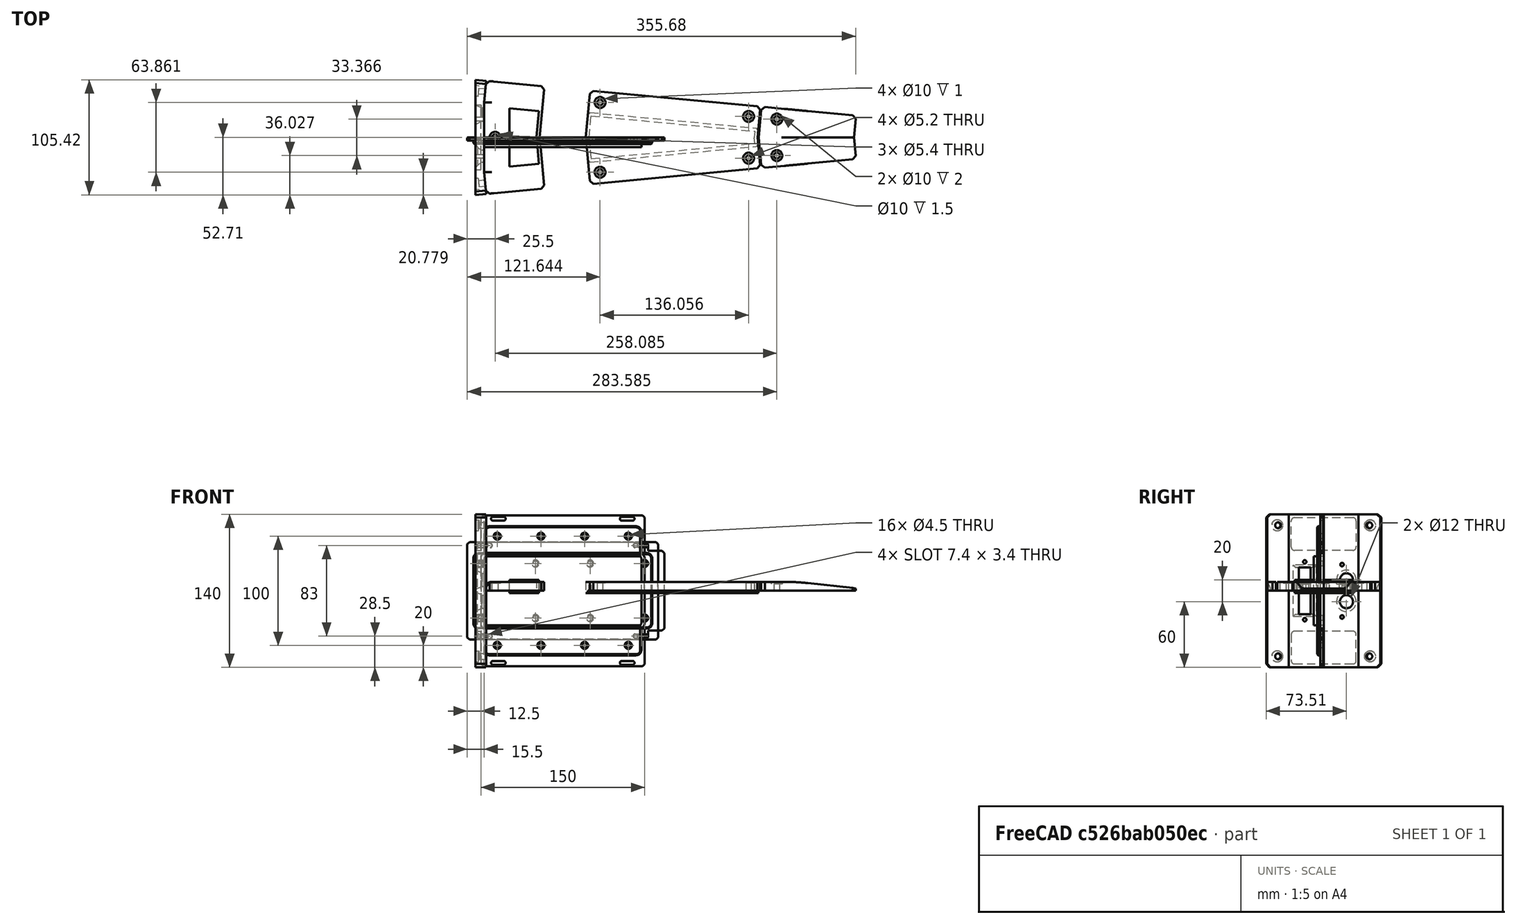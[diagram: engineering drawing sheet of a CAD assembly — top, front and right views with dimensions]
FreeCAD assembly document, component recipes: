
FREECAD ASSEMBLY — COMPONENT RECIPES ("RC-Robot-carters")

This assembly document has 8 components, labeled P0..P7 below (a component is one placed body or linked part). 8 of them carry a construction recipe — the FreeCAD feature program that regenerates the part from scratch, quoted from this document or its linked companion documents; the rest are supplied as boundary geometry only. No exploded tour is included for this assembly.
COMPONENT P0 — recipe-attached ("front-carter", modeled in this document).
Construction recipe (the document's own serialized feature program — sketch geometry with constraints, then the solid features built on it; lengths are millimeters unless a unit is written):

FEATURE [PartDesign::SubShapeBinder] Binder002
  BindCopyOnChange = 0
  BindMode = 0
  ClaimChildren = false
  Context = -> Body002 [Binder002.]
  Fuse = false
  MakeFace = true
  OffsetFill = false
  OffsetIntersection = false
  OffsetJoinType = 0
  OffsetOpenResult = false
  PartialLoad = false
  Refine = true
  Relative = true
  Support = -> [Link]
  _Version = 2
FEATURE [PartDesign::SubShapeBinder] Binder003
  BindCopyOnChange = 0
  BindMode = 0
  ClaimChildren = false
  Context = -> Body002 [Binder003.]
  Fuse = false
  MakeFace = true
  OffsetFill = false
  OffsetIntersection = false
  OffsetJoinType = 0
  OffsetOpenResult = false
  PartialLoad = false
  Refine = true
  Relative = true
  Support = -> [Part[Body.Mirrored.Face32]]
  _Version = 2
FEATURE [Sketcher::SketchObject] Sketch004
  ArcFitTolerance = 1e-06
  AttachmentSupport = -> [Origin006]
  ExternalGeometry = -> [Binder002,Binder003]
  ExternalTypes = [0,0,0,0,0,0]
  FullyConstrained = true
  MakeInternals = false
  MapMode = 5
  sketch-geometry (7):
    g0: LineSegment StartX=268.466 StartY=19.9119 StartZ=0 EndX=182.088 EndY=28.0449 EndZ=0
    g1: LineSegment StartX=182.088 StartY=28.0449 StartZ=0 EndX=179.448 EndY=0 EndZ=0
    g2: LineSegment StartX=179.448 StartY=0 StartZ=0 EndX=266.591 EndY=0 EndZ=0
    g3: LineSegment StartX=266.591 StartY=0 StartZ=0 EndX=268.466 EndY=19.9119 EndZ=0
    g4: Circle CenterX=196.085 CenterY=16.6828 CenterZ=0 NormalX=0 NormalY=0 NormalZ=1 AngleXU=0 Radius=2.7
    g5: GeomPoint X=180.214 Y=8.13298 Z=0
    g6: LineSegment [constr] StartX=196.085 StartY=16.6828 StartZ=0 EndX=197.022 EndY=26.6388 EndZ=0
  constraints (19):
    c: PointOnObject(g0,g-5)
    c: Coincident(g0,g1)
    c: PointOnObject(g1,g-1)
    c: Coincident(g2,g1)
    c: Coincident(g2,g-5)
    c: Coincident(g3,g2)
    c: Coincident(g3,g0)
    c: Parallel(g0,g-6)
    c: Perpendicular(g0,g1)
    c: Distance(g1,g-8) = 1
    c: Distance(g3,g3) = 20
    c: Diameter(g4) = 5.4
    c: PointOnObject(g5,g-3)
    c: PointOnObject(g5,g1)
    c: Coincident(g6,g4)
    c: Distance(g6,g6) = 10
    c: Perpendicular(g0,g6)
    c: PointOnObject(g6,g0)
    c: Distance(g6,g1) = 15
FEATURE [PartDesign::Pad] Pad003
  Direction = (0,0,1)
  Length = 8.2
  Length2 = 10
  Profile = -> Sketch004
  ReferenceAxis = -> Sketch004 [N_Axis]
  Refine = true
  SideType = 0
  Suppressed = false
  Type = 0
  Type2 = 0
FEATURE [Sketcher::SketchObject] Sketch005
  ArcFitTolerance = 1e-06
  AttachmentSupport = -> [Pad003]
  ExternalGeometry = -> [Pad003]
  ExternalTypes = [0]
  FullyConstrained = true
  MakeInternals = false
  MapMode = 5
  Placement = pos=(0,0,8.2) rot=(0,0,1;0rad)
  sketch-geometry (1):
    g0: Circle CenterX=196.085 CenterY=16.6828 CenterZ=0 NormalX=0 NormalY=0 NormalZ=1 AngleXU=0 Radius=5
  constraints (2):
    c: Coincident(g0,g-3)
    c: Diameter(g0) = 10
FEATURE [PartDesign::Pocket] Pocket001
  BaseFeature = -> Pad003
  Direction = (0,0,-1)
  Length = 2
  Length2 = 5
  Profile = -> Sketch005
  ReferenceAxis = -> Sketch005 [N_Axis]
  Refine = true
  SideType = 0
  Suppressed = false
  Type = 0
  Type2 = 0
FEATURE [PartDesign::Chamfer] Chamfer002
  Angle = 45
  Base = -> Pocket001 [Edge2]
  BaseFeature = -> Pocket001
  ChamferType = 0
  FlipDirection = false
  Refine = true
  Size = 3
  Size2 = 1
  SupportTransform = false
  Suppressed = false
  UseAllEdges = false
FEATURE [PartDesign::Chamfer] Chamfer003
  Angle = 45
  Base = -> Chamfer002 [Edge13]
  BaseFeature = -> Chamfer002
  ChamferType = 1
  FlipDirection = false
  Refine = true
  Size = 6
  Size2 = 55
  SupportTransform = false
  Suppressed = false
  UseAllEdges = false
FEATURE [PartDesign::Fillet] Fillet
  Base = -> Chamfer003 [Edge10]
  BaseFeature = -> Chamfer003
  Radius = 200
  Refine = true
  SupportTransform = false
  Suppressed = false
  UseAllEdges = false
FEATURE [PartDesign::Chamfer] Chamfer004
  Angle = 45
  Base = -> Fillet [Edge3]
  BaseFeature = -> Fillet
  ChamferType = 0
  FlipDirection = false
  Refine = true
  Size = 3
  Size2 = 1
  SupportTransform = false
  Suppressed = false
  UseAllEdges = false
FEATURE [PartDesign::Mirrored] Mirrored001
  BaseFeature = -> Chamfer004
  MirrorPlane = -> Chamfer004 [Face9]
  Refine = true
  Suppressed = false
  TransformMode = 1
FEATURE [PartDesign::Body] Body002  label="front-carter"
  AllowCompound = true
  Group = -> [Binder002,Sketch004,Binder003,Pad003,Sketch005,Pocket001,Chamfer002,Chamfer003,Fillet,Chamfer004,Mirrored001]
  Origin = -> Origin006
  Tip = -> Mirrored001
COMPONENT P1 — recipe-attached ("top-carter-core001", modeled in this document).
Construction recipe (the document's own serialized feature program — sketch geometry with constraints, then the solid features built on it; lengths are millimeters unless a unit is written):

FEATURE [Sketcher::SketchObject] Sketch022
  ArcFitTolerance = 1e-06
  AttachmentSupport = -> [Origin026]
  ExternalTypes = [0]
  FullyConstrained = true
  MakeInternals = false
  MapMode = 5
  Placement = pos=(0,0,0) rot=(1,0,0;1.5708rad)
  sketch-geometry (13):
    g0: LineSegment [constr] StartX=-87.5 StartY=-45 StartZ=0 EndX=87.5 EndY=-45 EndZ=0
    g1: LineSegment [constr] StartX=87.5 StartY=-45 StartZ=0 EndX=87.5 EndY=45 EndZ=0
    g2: LineSegment [constr] StartX=87.5 StartY=45 StartZ=0 EndX=-87.5 EndY=45 EndZ=0
    g3: LineSegment [constr] StartX=-87.5 StartY=45 StartZ=0 EndX=-87.5 EndY=-45 EndZ=0
    g4: GeomPoint [constr] X=0 Y=0 Z=0
    g5: LineSegment [constr] StartX=-87.5 StartY=-44.6 StartZ=0 EndX=87.5 EndY=-44.6 EndZ=0
    g6: LineSegment StartX=87.5 StartY=-44.6 StartZ=0 EndX=87.5 EndY=44.6 EndZ=0
    g7: LineSegment [constr] StartX=87.5 StartY=44.6 StartZ=0 EndX=-87.5 EndY=44.6 EndZ=0
    g8: LineSegment [constr] StartX=-87.5 StartY=44.6 StartZ=0 EndX=-87.5 EndY=-44.6 EndZ=0
    g9: GeomPoint [constr] X=0 Y=0 Z=0
    g10: LineSegment StartX=-2e-15 StartY=-44.6 StartZ=0 EndX=-2e-15 EndY=44.6 EndZ=0
    g11: LineSegment StartX=-2e-15 StartY=44.6 StartZ=0 EndX=87.5 EndY=44.6 EndZ=0
    g12: LineSegment StartX=-2e-15 StartY=-44.6 StartZ=0 EndX=87.5 EndY=-44.6 EndZ=0
  constraints (30):
    c: Coincident(g0,g1)
    c: Coincident(g1,g2)
    c: Coincident(g2,g3)
    c: Coincident(g3,g0)
    c: Horizontal(g0)
    c: Horizontal(g2)
    c: Vertical(g1)
    c: Vertical(g3)
    c: Symmetric(g2,g0,g4)
    c: Coincident(g4,g-1)
    c: DistanceX(g2,g2) = 175
    c: DistanceY(g1,g1) = 90
    c: Coincident(g5,g6)
    c: Coincident(g6,g7)
    c: Coincident(g7,g8)
    c: Coincident(g8,g5)
    c: Horizontal(g5)
    c: Horizontal(g7)
    c: Vertical(g6)
    c: Vertical(g8)
    c: Symmetric(g7,g5,g9)
    c: Coincident(g9,g4)
    c: PointOnObject(g6,g1)
    c: Distance(g6,g1) = 0.4
    c: Symmetric(g5,g5,g10)
    c: Symmetric(g7,g7,g10)
    c: Coincident(g11,g10)
    c: Coincident(g11,g6)
    c: Coincident(g12,g10)
    c: Coincident(g12,g5)
FEATURE [PartDesign::Pad] Pad013
  Direction = (0,-1,2e-16)
  Length = 3
  Length2 = 10
  Profile = -> Sketch022
  ReferenceAxis = -> Sketch022 [N_Axis]
  Refine = true
  SideType = 0
  Suppressed = false
  Type = 0
  Type2 = 0
FEATURE [Sketcher::SketchObject] Sketch023
  ArcFitTolerance = 1e-06
  AttachmentSupport = -> [Origin026]
  ExternalGeometry = -> [Pad013]
  ExternalTypes = [0,0]
  FullyConstrained = true
  MakeInternals = false
  MapMode = 5
  Placement = pos=(0,0,0) rot=(1,0,0;1.5708rad)
  sketch-geometry (6):
    g0: ArcOfCircle CenterX=76.5 CenterY=41.5 CenterZ=0 NormalX=0 NormalY=0 NormalZ=1 AngleXU=0 Radius=1.7 StartAngle=4.71239 EndAngle=7.85398
    g1: ArcOfCircle CenterX=66.5 CenterY=41.5 CenterZ=0 NormalX=0 NormalY=0 NormalZ=1 AngleXU=0 Radius=1.7 StartAngle=1.5708 EndAngle=4.71239
    g2: LineSegment StartX=76.5 StartY=39.8 StartZ=0 EndX=66.5 EndY=39.8 EndZ=0
    g3: LineSegment StartX=76.5 StartY=43.2 StartZ=0 EndX=66.5 EndY=43.2 EndZ=0
    g4: LineSegment [constr] StartX=66.5 StartY=41.5 StartZ=0 EndX=76.5 EndY=41.5 EndZ=0
    g5: GeomPoint [constr] X=71.5 Y=41.5 Z=0
  constraints (13):
    c: Tangent(g0,g2) = 1.5708
    c: Tangent(g0,g3) = -1.5708
    c: Tangent(g1,g2) = 1.5708
    c: Tangent(g1,g3) = -1.5708
    c: Equal(g0,g1)
    c: Horizontal(g3)
    c: DistanceX(g1,g0) = 10
    c: Radius(g0) = 1.7
    c: DistanceY(g-1,g0) = 41.5
    c: Coincident(g4,g1)
    c: Coincident(g4,g0)
    c: Symmetric(g4,g4,g5)
    c: Distance(g5,g-3) = 16
FEATURE [PartDesign::Pocket] Pocket010
  BaseFeature = -> Pad013
  Direction = (0,1,-2e-16)
  Length = 5
  Length2 = 5
  Profile = -> Sketch023
  ReferenceAxis = -> Sketch023 [N_Axis]
  Refine = true
  Reversed = true
  SideType = 0
  Suppressed = false
  Type = 0
  Type2 = 0
FEATURE [PartDesign::Mirrored] Mirrored008
  BaseFeature = -> Pocket010
  MirrorPlane = -> XY_Plane013
  Originals = -> [Pocket010]
  Refine = true
  Suppressed = false
  TransformMode = 0
FEATURE [PartDesign::Mirrored] Mirrored009
  BaseFeature = -> Mirrored008
  MirrorPlane = -> YZ_Plane013
  Refine = true
  Suppressed = false
  TransformMode = 1
FEATURE [PartDesign::Chamfer] Chamfer013
  Angle = 45
  Base = -> Mirrored009 [Edge8,Edge6,Edge2,Edge1]
  BaseFeature = -> Mirrored009
  ChamferType = 0
  FlipDirection = false
  Refine = true
  Size = 2
  Size2 = 1
  SupportTransform = false
  Suppressed = false
  UseAllEdges = false
FEATURE [Sketcher::SketchObject] Sketch025
  ArcFitTolerance = 1e-06
  ExternalTypes = [0,0]
  FullyConstrained = true
  MakeInternals = false
  MapMode = 5
  Placement = pos=(0,-3,0) rot=(1,0,0;1.5708rad)
  sketch-geometry (5):
    g0: LineSegment StartX=-82 StartY=-34.6 StartZ=0 EndX=82 EndY=-34.6 EndZ=0
    g1: LineSegment StartX=82 StartY=-34.6 StartZ=0 EndX=82 EndY=34.6 EndZ=0
    g2: LineSegment StartX=82 StartY=34.6 StartZ=0 EndX=-82 EndY=34.6 EndZ=0
    g3: LineSegment StartX=-82 StartY=34.6 StartZ=0 EndX=-82 EndY=-34.6 EndZ=0
    g4: GeomPoint [constr] X=0 Y=0 Z=0
  constraints (12):
    c: Coincident(g0,g1)
    c: Coincident(g1,g2)
    c: Coincident(g2,g3)
    c: Coincident(g3,g0)
    c: Horizontal(g0)
    c: Horizontal(g2)
    c: Vertical(g1)
    c: Vertical(g3)
    c: Symmetric(g2,g0,g4)
    c: Coincident(g4,g-1)
    c: Distance(g-3,g3) = 3
    c: Distance(g-4,g2) = 10
FEATURE [PartDesign::Pad] Pad015
  BaseFeature = -> Chamfer013
  Direction = (0,-1,2e-16)
  Length = 3
  Length2 = 10
  Profile = -> Sketch025
  ReferenceAxis = -> Sketch025 [N_Axis]
  Refine = true
  SideType = 0
  Suppressed = false
  Type = 0
  Type2 = 0
FEATURE [PartDesign::Fillet] Fillet004
  Base = -> Pad015 [Edge80,Edge78,Edge82,Edge77]
  BaseFeature = -> Pad015
  Radius = 5
  Refine = true
  SupportTransform = false
  Suppressed = false
  UseAllEdges = false
FEATURE [Sketcher::SketchObject] Sketch026
  ArcFitTolerance = 1e-06
  AttachmentSupport = -> [Fillet004]
  ExternalTypes = [0]
  FullyConstrained = true
  MakeInternals = true
  MapMode = 5
  Placement = pos=(0,-6,0) rot=(1,0,0;1.5708rad)
  sketch-geometry (19):
    g0: LineSegment [constr] StartX=-75 StartY=25 StartZ=0 EndX=-75 EndY=-25 EndZ=0
    g1: LineSegment [constr] StartX=-75 StartY=-25 StartZ=0 EndX=-25 EndY=-25 EndZ=0
    g2: LineSegment [constr] StartX=-25 StartY=-25 StartZ=0 EndX=-25 EndY=25 EndZ=0
    g3: LineSegment [constr] StartX=-25 StartY=25 StartZ=0 EndX=-75 EndY=25 EndZ=0
    g4: GeomPoint [constr] X=-50 Y=0 Z=0
    g5: LineSegment [constr] StartX=25 StartY=25 StartZ=0 EndX=25 EndY=-25 EndZ=0
    g6: LineSegment [constr] StartX=25 StartY=-25 StartZ=0 EndX=75 EndY=-25 EndZ=0
    g7: LineSegment [constr] StartX=75 StartY=-25 StartZ=0 EndX=75 EndY=25 EndZ=0
    g8: LineSegment [constr] StartX=75 StartY=25 StartZ=0 EndX=25 EndY=25 EndZ=0
    g9: GeomPoint [constr] X=50 Y=0 Z=0
    g10: LineSegment [constr] StartX=-25 StartY=25 StartZ=0 EndX=25 EndY=25 EndZ=0
    g11: Circle CenterX=-75 CenterY=25 CenterZ=0 NormalX=0 NormalY=0 NormalZ=1 AngleXU=0 Radius=2.25
    g12: Circle CenterX=-25 CenterY=25 CenterZ=0 NormalX=0 NormalY=0 NormalZ=1 AngleXU=0 Radius=2.25
    g13: Circle CenterX=25 CenterY=25 CenterZ=0 NormalX=0 NormalY=0 NormalZ=1 AngleXU=0 Radius=2.25
    g14: Circle CenterX=75 CenterY=25 CenterZ=0 NormalX=0 NormalY=0 NormalZ=1 AngleXU=0 Radius=2.25
    g15: Circle CenterX=75 CenterY=-25 CenterZ=0 NormalX=0 NormalY=0 NormalZ=1 AngleXU=0 Radius=2.25
    g16: Circle CenterX=25 CenterY=-25 CenterZ=0 NormalX=0 NormalY=0 NormalZ=1 AngleXU=0 Radius=2.25
    g17: Circle CenterX=-25 CenterY=-25 CenterZ=0 NormalX=0 NormalY=0 NormalZ=1 AngleXU=0 Radius=2.25
    g18: Circle CenterX=-75 CenterY=-25 CenterZ=0 NormalX=0 NormalY=0 NormalZ=1 AngleXU=0 Radius=2.25
  constraints (43):
    c: Coincident(g0,g1)
    c: Coincident(g1,g2)
    c: Coincident(g2,g3)
    c: Coincident(g3,g0)
    c: Vertical(g0)
    c: Vertical(g2)
    c: Horizontal(g1)
    c: Horizontal(g3)
    c: Symmetric(g2,g0,g4)
    c: PointOnObject(g4,g-1)
    c: Coincident(g5,g6)
    c: Coincident(g6,g7)
    c: Coincident(g7,g8)
    c: Coincident(g8,g5)
    c: Vertical(g5)
    c: Vertical(g7)
    c: Horizontal(g6)
    c: Horizontal(g8)
    c: Symmetric(g7,g5,g9)
    c: PointOnObject(g9,g-1)
    c: Symmetric(g2,g5,g-2)
    c: Equal(g3,g5)
    c: Equal(g5,g8)
    c: Coincident(g10,g2)
    c: Coincident(g10,g5)
    c: Equal(g10,g8)
    c: DistanceY(g7,g7) = 50
    c: Coincident(g11,g0)
    c: Coincident(g12,g2)
    c: Coincident(g13,g5)
    c: Coincident(g14,g7)
    c: Coincident(g15,g6)
    c: Coincident(g16,g5)
    c: Coincident(g17,g1)
    c: Coincident(g18,g0)
    c: Equal(g18,g11)
    c: Equal(g11,g12)
    c: Equal(g12,g17)
    c: Equal(g17,g13)
    c: Equal(g13,g16)
    c: Equal(g16,g15)
    c: Equal(g15,g14)
    c: Diameter(g14) = 4.5
FEATURE [PartDesign::Pocket] Pocket011
  BaseFeature = -> Fillet004
  Direction = (0,1,-2e-16)
  Length = 7
  Length2 = 5
  Profile = -> Sketch026
  ReferenceAxis = -> Sketch026 [N_Axis]
  Refine = true
  SideType = 0
  Suppressed = false
  Type = 0
  Type2 = 0
FEATURE [PartDesign::Chamfer] Chamfer014
  Angle = 45
  Base = -> Pocket011 [Face34]
  BaseFeature = -> Pocket011
  ChamferType = 0
  FlipDirection = false
  Refine = true
  Size = 1
  Size2 = 1
  SupportTransform = false
  Suppressed = false
  UseAllEdges = false
FEATURE [PartDesign::Chamfer] Chamfer015
  Angle = 45
  Base = -> Chamfer014 [Face51]
  BaseFeature = -> Chamfer014
  ChamferType = 0
  FlipDirection = false
  Refine = true
  Size = 0.4
  Size2 = 1
  SupportTransform = false
  Suppressed = false
  UseAllEdges = false
FEATURE [PartDesign::Body] Body009  label="top-carter-core001"
  AllowCompound = true
  Group = -> [Sketch022,Pad013,Sketch023,Pocket010,Mirrored008,Mirrored009,Chamfer013,Sketch025,Pad015,Fillet004,Sketch026,Pocket011,Chamfer014,Chamfer015]
  Origin = -> Origin026
  Tip = -> Chamfer015
COMPONENT P2 — recipe-attached ("top-carter-core002", modeled in this document).
Construction recipe (the document's own serialized feature program — sketch geometry with constraints, then the solid features built on it; lengths are millimeters unless a unit is written):

FEATURE [Sketcher::SketchObject] Sketch027
  ArcFitTolerance = 1e-06
  AttachmentSupport = -> [Origin028]
  ExternalTypes = [0]
  FullyConstrained = true
  MakeInternals = false
  MapMode = 5
  Placement = pos=(0,0,0) rot=(1,0,0;1.5708rad)
  sketch-geometry (13):
    g0: LineSegment [constr] StartX=-75 StartY=-69.5 StartZ=0 EndX=75 EndY=-69.5 EndZ=0
    g1: LineSegment [constr] StartX=75 StartY=-69.5 StartZ=0 EndX=75 EndY=69.5 EndZ=0
    g2: LineSegment [constr] StartX=75 StartY=69.5 StartZ=0 EndX=-75 EndY=69.5 EndZ=0
    g3: LineSegment [constr] StartX=-75 StartY=69.5 StartZ=0 EndX=-75 EndY=-69.5 EndZ=0
    g4: GeomPoint [constr] X=0 Y=0 Z=0
    g5: LineSegment [constr] StartX=-75 StartY=-69.1 StartZ=0 EndX=75 EndY=-69.1 EndZ=0
    g6: LineSegment StartX=75 StartY=-69.1 StartZ=0 EndX=75 EndY=69.1 EndZ=0
    g7: LineSegment [constr] StartX=75 StartY=69.1 StartZ=0 EndX=-75 EndY=69.1 EndZ=0
    g8: LineSegment [constr] StartX=-75 StartY=69.1 StartZ=0 EndX=-75 EndY=-69.1 EndZ=0
    g9: GeomPoint [constr] X=0 Y=0 Z=0
    g10: LineSegment StartX=3.7e-15 StartY=-69.1 StartZ=0 EndX=3.7e-15 EndY=69.1 EndZ=0
    g11: LineSegment StartX=3.7e-15 StartY=69.1 StartZ=0 EndX=75 EndY=69.1 EndZ=0
    g12: LineSegment StartX=3.7e-15 StartY=-69.1 StartZ=0 EndX=75 EndY=-69.1 EndZ=0
  constraints (30):
    c: Coincident(g0,g1)
    c: Coincident(g1,g2)
    c: Coincident(g2,g3)
    c: Coincident(g3,g0)
    c: Horizontal(g0)
    c: Horizontal(g2)
    c: Vertical(g1)
    c: Vertical(g3)
    c: Symmetric(g2,g0,g4)
    c: Coincident(g4,g-1)
    c: DistanceX(g2,g2) = 150
    c: DistanceY(g1,g1) = 139
    c: Coincident(g5,g6)
    c: Coincident(g6,g7)
    c: Coincident(g7,g8)
    c: Coincident(g8,g5)
    c: Horizontal(g5)
    c: Horizontal(g7)
    c: Vertical(g6)
    c: Vertical(g8)
    c: Symmetric(g7,g5,g9)
    c: Coincident(g9,g4)
    c: PointOnObject(g6,g1)
    c: Distance(g6,g1) = 0.4
    c: Symmetric(g5,g5,g10)
    c: Symmetric(g7,g7,g10)
    c: Coincident(g11,g10)
    c: Coincident(g11,g6)
    c: Coincident(g12,g10)
    c: Coincident(g12,g5)
FEATURE [PartDesign::Pad] Pad016
  Direction = (0,-1,2e-16)
  Length = 3
  Length2 = 10
  Profile = -> Sketch027
  ReferenceAxis = -> Sketch027 [N_Axis]
  Refine = true
  SideType = 0
  Suppressed = false
  Type = 0
  Type2 = 0
FEATURE [Sketcher::SketchObject] Sketch028
  ArcFitTolerance = 1e-06
  AttachmentSupport = -> [Origin028]
  ExternalGeometry = -> [Pad016]
  ExternalTypes = [0,0]
  FullyConstrained = true
  MakeInternals = false
  MapMode = 5
  Placement = pos=(0,0,0) rot=(1,0,0;1.5708rad)
  sketch-geometry (6):
    g0: ArcOfCircle CenterX=64 CenterY=66 CenterZ=0 NormalX=0 NormalY=0 NormalZ=1 AngleXU=0 Radius=1.7 StartAngle=4.71239 EndAngle=7.85398
    g1: ArcOfCircle CenterX=54 CenterY=66 CenterZ=0 NormalX=0 NormalY=0 NormalZ=1 AngleXU=0 Radius=1.7 StartAngle=1.5708 EndAngle=4.71239
    g2: LineSegment StartX=64 StartY=64.3 StartZ=0 EndX=54 EndY=64.3 EndZ=0
    g3: LineSegment StartX=64 StartY=67.7 StartZ=0 EndX=54 EndY=67.7 EndZ=0
    g4: LineSegment [constr] StartX=54 StartY=66 StartZ=0 EndX=64 EndY=66 EndZ=0
    g5: GeomPoint [constr] X=59 Y=66 Z=0
  constraints (13):
    c: Tangent(g0,g2) = 1.5708
    c: Tangent(g0,g3) = -1.5708
    c: Tangent(g1,g2) = 1.5708
    c: Tangent(g1,g3) = -1.5708
    c: Equal(g0,g1)
    c: Horizontal(g3)
    c: DistanceX(g1,g0) = 10
    c: Radius(g0) = 1.7
    c: Coincident(g4,g1)
    c: Coincident(g4,g0)
    c: Symmetric(g4,g4,g5)
    c: Distance(g5,g-3) = 16
    c: Distance(g-4,g4) = 3.1
FEATURE [PartDesign::Pocket] Pocket012
  BaseFeature = -> Pad016
  Direction = (0,1,-2e-16)
  Length = 5
  Length2 = 5
  Profile = -> Sketch028
  ReferenceAxis = -> Sketch028 [N_Axis]
  Refine = true
  Reversed = true
  SideType = 0
  Suppressed = false
  Type = 0
  Type2 = 0
FEATURE [PartDesign::Mirrored] Mirrored010
  BaseFeature = -> Pocket012
  MirrorPlane = -> XY_Plane014
  Originals = -> [Pocket012]
  Refine = true
  Suppressed = false
  TransformMode = 0
FEATURE [PartDesign::Mirrored] Mirrored011
  BaseFeature = -> Mirrored010
  MirrorPlane = -> YZ_Plane014
  Refine = true
  Suppressed = false
  TransformMode = 1
FEATURE [PartDesign::Chamfer] Chamfer016
  Angle = 45
  Base = -> Mirrored011 [Edge6,Edge1,Edge8,Edge2]
  BaseFeature = -> Mirrored011
  ChamferType = 0
  FlipDirection = false
  Refine = true
  Size = 2
  Size2 = 1
  SupportTransform = false
  Suppressed = false
  UseAllEdges = false
FEATURE [Sketcher::SketchObject] Sketch029
  ArcFitTolerance = 1e-06
  AttachmentSupport = -> [Chamfer016]
  ExternalGeometry = -> [Chamfer016]
  ExternalTypes = [0,0]
  FullyConstrained = true
  MakeInternals = false
  MapMode = 5
  Placement = pos=(0,-3,7e-16) rot=(1,0,0;1.5708rad)
  sketch-geometry (5):
    g0: LineSegment StartX=-72 StartY=-59.1 StartZ=0 EndX=72 EndY=-59.1 EndZ=0
    g1: LineSegment StartX=72 StartY=-59.1 StartZ=0 EndX=72 EndY=59.1 EndZ=0
    g2: LineSegment StartX=72 StartY=59.1 StartZ=0 EndX=-72 EndY=59.1 EndZ=0
    g3: LineSegment StartX=-72 StartY=59.1 StartZ=0 EndX=-72 EndY=-59.1 EndZ=0
    g4: GeomPoint [constr] X=0 Y=0 Z=0
  constraints (12):
    c: Coincident(g0,g1)
    c: Coincident(g1,g2)
    c: Coincident(g2,g3)
    c: Coincident(g3,g0)
    c: Horizontal(g0)
    c: Horizontal(g2)
    c: Vertical(g1)
    c: Vertical(g3)
    c: Symmetric(g2,g0,g4)
    c: Coincident(g4,g-1)
    c: Distance(g-3,g2) = 10
    c: Distance(g-4,g3) = 3
FEATURE [PartDesign::Pad] Pad017
  BaseFeature = -> Chamfer016
  Direction = (0,-1,2e-16)
  Length = 3
  Length2 = 10
  Profile = -> Sketch029
  ReferenceAxis = -> Sketch029 [N_Axis]
  Refine = true
  SideType = 0
  Suppressed = false
  Type = 0
  Type2 = 0
FEATURE [PartDesign::Fillet] Fillet005
  Base = -> Pad017 [Edge78,Edge80,Edge77,Edge82]
  BaseFeature = -> Pad017
  Radius = 5
  Refine = true
  SupportTransform = false
  Suppressed = false
  UseAllEdges = false
FEATURE [Sketcher::SketchObject] Sketch030
  ArcFitTolerance = 1e-06
  AttachmentSupport = -> [Fillet005]
  ExternalGeometry = -> [Fillet005]
  ExternalTypes = [0,0]
  FullyConstrained = true
  MakeInternals = true
  MapMode = 5
  Placement = pos=(0,-6,1.4e-15) rot=(1,0,0;1.5708rad)
  sketch-geometry (19):
    g0: LineSegment [constr] StartX=-60 StartY=50 StartZ=0 EndX=-60 EndY=-50 EndZ=0
    g1: LineSegment [constr] StartX=-60 StartY=-50 StartZ=0 EndX=-20 EndY=-50 EndZ=0
    g2: LineSegment [constr] StartX=-20 StartY=-50 StartZ=0 EndX=-20 EndY=50 EndZ=0
    g3: LineSegment [constr] StartX=-20 StartY=50 StartZ=0 EndX=-60 EndY=50 EndZ=0
    g4: GeomPoint [constr] X=-40 Y=0 Z=0
    g5: LineSegment [constr] StartX=20 StartY=50 StartZ=0 EndX=20 EndY=-50 EndZ=0
    g6: LineSegment [constr] StartX=20 StartY=-50 StartZ=0 EndX=60 EndY=-50 EndZ=0
    g7: LineSegment [constr] StartX=60 StartY=-50 StartZ=0 EndX=60 EndY=50 EndZ=0
    g8: LineSegment [constr] StartX=60 StartY=50 StartZ=0 EndX=20 EndY=50 EndZ=0
    g9: GeomPoint [constr] X=40 Y=0 Z=0
    g10: LineSegment [constr] StartX=-20 StartY=50 StartZ=0 EndX=20 EndY=50 EndZ=0
    g11: Circle CenterX=-60 CenterY=50 CenterZ=0 NormalX=0 NormalY=0 NormalZ=1 AngleXU=0 Radius=2.25
    g12: Circle CenterX=-20 CenterY=50 CenterZ=0 NormalX=0 NormalY=0 NormalZ=1 AngleXU=0 Radius=2.25
    g13: Circle CenterX=20 CenterY=50 CenterZ=0 NormalX=0 NormalY=0 NormalZ=1 AngleXU=0 Radius=2.25
    g14: Circle CenterX=60 CenterY=50 CenterZ=0 NormalX=0 NormalY=0 NormalZ=1 AngleXU=0 Radius=2.25
    g15: Circle CenterX=60 CenterY=-50 CenterZ=0 NormalX=0 NormalY=0 NormalZ=1 AngleXU=0 Radius=2.25
    g16: Circle CenterX=20 CenterY=-50 CenterZ=0 NormalX=0 NormalY=0 NormalZ=1 AngleXU=0 Radius=2.25
    g17: Circle CenterX=-20 CenterY=-50 CenterZ=0 NormalX=0 NormalY=0 NormalZ=1 AngleXU=0 Radius=2.25
    g18: Circle CenterX=-60 CenterY=-50 CenterZ=0 NormalX=0 NormalY=0 NormalZ=1 AngleXU=0 Radius=2.25
  constraints (43):
    c: Coincident(g0,g1)
    c: Coincident(g1,g2)
    c: Coincident(g2,g3)
    c: Coincident(g3,g0)
    c: Vertical(g0)
    c: Vertical(g2)
    c: Horizontal(g1)
    c: Horizontal(g3)
    c: Symmetric(g2,g0,g4)
    c: PointOnObject(g4,g-1)
    c: Coincident(g5,g6)
    c: Coincident(g6,g7)
    c: Coincident(g7,g8)
    c: Coincident(g8,g5)
    c: Vertical(g5)
    c: Vertical(g7)
    c: Horizontal(g6)
    c: Horizontal(g8)
    c: Symmetric(g7,g5,g9)
    c: PointOnObject(g9,g-1)
    c: Symmetric(g2,g5,g-2)
    c: Coincident(g10,g2)
    c: Coincident(g10,g5)
    c: Equal(g10,g8)
    c: DistanceY(g7,g7) = 100
    c: Coincident(g11,g0)
    c: Coincident(g12,g2)
    c: Coincident(g13,g5)
    c: Coincident(g14,g7)
    c: Coincident(g15,g6)
    c: Coincident(g16,g5)
    c: Coincident(g17,g1)
    c: Coincident(g18,g0)
    c: Equal(g18,g11)
    c: Equal(g11,g12)
    c: Equal(g12,g17)
    c: Equal(g17,g13)
    c: Equal(g13,g16)
    c: Equal(g16,g15)
    c: Equal(g15,g14)
    c: Diameter(g14) = 4.5
    c: Equal(g3,g10)
    c: DistanceX(g8,g8) = 40
FEATURE [PartDesign::Pocket] Pocket013
  BaseFeature = -> Fillet005
  Direction = (0,1,-2e-16)
  Length = 7
  Length2 = 5
  Profile = -> Sketch030
  ReferenceAxis = -> Sketch030 [N_Axis]
  Refine = true
  SideType = 0
  Suppressed = false
  Type = 0
  Type2 = 0
FEATURE [PartDesign::Chamfer] Chamfer017
  Angle = 45
  Base = -> Pocket013 [Face34]
  BaseFeature = -> Pocket013
  ChamferType = 0
  FlipDirection = false
  Refine = true
  Size = 1
  Size2 = 1
  SupportTransform = false
  Suppressed = false
  UseAllEdges = false
FEATURE [PartDesign::Chamfer] Chamfer018
  Angle = 45
  Base = -> Chamfer017 [Face51]
  BaseFeature = -> Chamfer017
  ChamferType = 0
  FlipDirection = false
  Refine = true
  Size = 0.4
  Size2 = 1
  SupportTransform = false
  Suppressed = false
  UseAllEdges = false
FEATURE [PartDesign::Body] Body010  label="top-carter-core002"
  AllowCompound = true
  Group = -> [Sketch027,Pad016,Sketch028,Pocket012,Mirrored010,Mirrored011,Chamfer016,Sketch029,Pad017,Fillet005,Sketch030,Pocket013,Chamfer017,Chamfer018]
  Origin = -> Origin028
  Tip = -> Chamfer018
COMPONENT P3 — recipe-attached ("support-power-switch", modeled in this document).
Construction recipe (the document's own serialized feature program — sketch geometry with constraints, then the solid features built on it; lengths are millimeters unless a unit is written):

FEATURE [PartDesign::SubShapeBinder] Binder
  BindCopyOnChange = 0
  BindMode = 0
  ClaimChildren = false
  Context = -> Body [Binder.]
  Fuse = false
  MakeFace = true
  OffsetFill = false
  OffsetIntersection = false
  OffsetJoinType = 0
  OffsetOpenResult = false
  PartialLoad = false
  Refine = true
  Relative = true
  Support = -> [Link]
  _Version = 2
FEATURE [Sketcher::SketchObject] Sketch
  ArcFitTolerance = 1e-06
  AttachmentSupport = -> [Origin]
  ExternalGeometry = -> [Binder]
  ExternalTypes = [0,0,0,0,0,0]
  FullyConstrained = true
  MakeInternals = false
  MapMode = 5
  sketch-geometry (13):
    g0: LineSegment [constr] StartX=20.0885 StartY=0 StartZ=0 EndX=24.4107 EndY=45.9046 EndZ=0
    g1: LineSegment [constr] StartX=20.0885 StartY=0 StartZ=0 EndX=24.4107 EndY=-45.9046 EndZ=0
    g2: LineSegment [constr] StartX=-15.4132 StartY=49.6542 StartZ=0 EndX=-20.0885 EndY=0 EndZ=0
    g3: LineSegment [constr] StartX=-20.0885 StartY=0 StartZ=0 EndX=-15.4132 EndY=-49.6542 EndZ=0
    g4: LineSegment [constr] StartX=-70.0371 StartY=51.7842 StartZ=0 EndX=268.466 EndY=19.9119 EndZ=0
    g5: LineSegment [constr] StartX=266.591 StartY=0 StartZ=0 EndX=268.466 EndY=19.9119 EndZ=0
    g6: LineSegment StartX=25.125 StartY=42.824 StartZ=0 EndX=21.0929 EndY=0 EndZ=0
    g7: LineSegment StartX=21.0929 StartY=0 StartZ=0 EndX=178.443 EndY=0 EndZ=0
    g8: LineSegment StartX=178.443 StartY=0 StartZ=0 EndX=181.093 EndY=28.1387 EndZ=0
    g9: LineSegment StartX=181.093 StartY=28.1387 StartZ=0 EndX=25.125 EndY=42.824 EndZ=0
    g10: Circle CenterX=34.1436 CenterY=31.9306 CenterZ=0 NormalX=0 NormalY=0 NormalZ=1 AngleXU=0 Radius=2.6
    g11: Circle CenterX=170.199 CenterY=19.1201 CenterZ=0 NormalX=0 NormalY=0 NormalZ=1 AngleXU=0 Radius=2.6
    g12: LineSegment [constr] StartX=34.1436 StartY=31.9306 StartZ=0 EndX=170.199 EndY=19.1201 EndZ=0
  constraints (38):
    c: PointOnObject(g0,g-1)
    c: PointOnObject(g0,g-3)
    c: Coincident(g1,g0)
    c: PointOnObject(g1,g-4)
    c: Perpendicular(g-4,g1)
    c: Perpendicular(g-3,g0)
    c: PointOnObject(g2,g-3)
    c: Coincident(g3,g2)
    c: PointOnObject(g3,g-4)
    c: Parallel(g2,g0)
    c: Parallel(g3,g1)
    c: Symmetric(g2,g0,g-1)
    c: Distance(g2,g0) = 40
    c: Coincident(g4,g-7)
    c: Coincident(g5,g-6)
    c: Coincident(g5,g4)
    c: Parallel(g4,g-3)
    c: PointOnObject(g4,g-8)
    c: PointOnObject(g6,g4)
    c: PointOnObject(g6,g-1)
    c: Coincident(g7,g6)
    c: PointOnObject(g7,g-1)
    c: Coincident(g8,g7)
    c: PointOnObject(g8,g4)
    c: Coincident(g9,g8)
    c: Coincident(g9,g6)
    c: Parallel(g6,g0)
    c: Parallel(g8,g6)
    c: Distance(g6,g0) = 1
    c: DistanceX(g6,g8) = 160
    c: Coincident(g12,g10)
    c: Coincident(g12,g11)
    c: Parallel(g12,g9)
    c: Equal(g11,g10)
    c: Diameter(g10) = 5.2
    c: Distance(g10,g6) = 10
    c: Distance(g11,g8) = 10
    c: Distance(g9,g12) = 10
FEATURE [PartDesign::Pad] Pad
  Direction = (0,0,1)
  Length = 8.2
  Length2 = 10
  Profile = -> Sketch
  ReferenceAxis = -> Sketch [N_Axis]
  Refine = true
  SideType = 0
  Suppressed = false
  Type = 0
  Type2 = 0
FEATURE [Sketcher::SketchObject] Sketch001
  ArcFitTolerance = 1e-06
  AttachmentSupport = -> [Pad]
  ExternalGeometry = -> [Pad,Binder]
  ExternalTypes = [0,0,0,0]
  FullyConstrained = true
  MakeInternals = false
  MapMode = 5
  Placement = pos=(0,0,0) rot=(1,0,0;3.14159rad)
  sketch-geometry (4):
    g0: LineSegment StartX=21.0929 StartY=0 StartZ=0 EndX=23.2502 EndY=-22.9121 EndZ=0
    g1: LineSegment StartX=23.2502 StartY=-22.9121 StartZ=0 EndX=179.218 EndY=-8.22672 EndZ=0
    g2: LineSegment StartX=179.218 StartY=-8.22672 StartZ=0 EndX=178.443 EndY=0 EndZ=0
    g3: LineSegment StartX=178.443 StartY=0 StartZ=0 EndX=21.0929 EndY=0 EndZ=0
  constraints (10):
    c: Coincident(g0,g-3)
    c: PointOnObject(g0,g-6)
    c: Coincident(g1,g0)
    c: PointOnObject(g1,g-6)
    c: Coincident(g2,g1)
    c: Coincident(g2,g-4)
    c: Coincident(g3,g2)
    c: Coincident(g3,g0)
    c: PointOnObject(g0,g-3)
    c: PointOnObject(g1,g-4)
FEATURE [PartDesign::Pad] Pad001
  BaseFeature = -> Pad
  Direction = (0,0,-1)
  Length = 2
  Length2 = 10
  Profile = -> Sketch001
  ReferenceAxis = -> Sketch001 [N_Axis]
  Refine = true
  SideType = 0
  Suppressed = false
  Type = 0
  Type2 = 0
FEATURE [Sketcher::SketchObject] Sketch002
  ArcFitTolerance = 1e-06
  AttachmentSupport = -> [Pad001]
  ExternalGeometry = -> [Pad001]
  ExternalTypes = [0,0]
  FullyConstrained = true
  MakeInternals = false
  MapMode = 5
  Placement = pos=(0,0,8.2) rot=(0,0,1;0rad)
  sketch-geometry (2):
    g0: Circle CenterX=34.1436 CenterY=31.9306 CenterZ=0 NormalX=0 NormalY=0 NormalZ=1 AngleXU=0 Radius=5
    g1: Circle CenterX=170.199 CenterY=19.1201 CenterZ=0 NormalX=0 NormalY=0 NormalZ=1 AngleXU=0 Radius=5
  constraints (4):
    c: Coincident(g0,g-3)
    c: Coincident(g1,g-4)
    c: Equal(g0,g1)
    c: Diameter(g1) = 10
FEATURE [PartDesign::Pocket] Pocket
  BaseFeature = -> Pad001
  Direction = (0,0,-1)
  Length = 1
  Length2 = 5
  Profile = -> Sketch002
  ReferenceAxis = -> Sketch002 [N_Axis]
  Refine = true
  SideType = 0
  Suppressed = false
  Type = 0
  Type2 = 0
FEATURE [PartDesign::Chamfer] Chamfer
  Angle = 45
  Base = -> Pocket [Edge1,Edge2]
  BaseFeature = -> Pocket
  ChamferType = 0
  FlipDirection = false
  Refine = true
  Size = 3
  Size2 = 1
  SupportTransform = false
  Suppressed = false
  UseAllEdges = false
FEATURE [PartDesign::Chamfer] Chamfer001
  Angle = 45
  Base = -> Chamfer [Edge21,Edge24]
  BaseFeature = -> Chamfer
  ChamferType = 0
  FlipDirection = false
  Refine = true
  Size = 2
  Size2 = 1
  SupportTransform = false
  Suppressed = false
  UseAllEdges = false
FEATURE [PartDesign::Mirrored] Mirrored
  BaseFeature = -> Chamfer001
  MirrorPlane = -> Chamfer001 [Face13]
  Refine = true
  Suppressed = false
  TransformMode = 1
FEATURE [PartDesign::Body] Body  label="lateral-carter-core"
  AllowCompound = true
  Group = -> [Binder,Sketch,Pad,Sketch001,Pad001,Sketch002,Pocket,Chamfer,Chamfer001,Mirrored]
  Origin = -> Origin
  Tip = -> Mirrored
COMPONENT P4 — recipe-attached ("lateral-carter", modeled in this document).
Construction recipe (the document's own serialized feature program — sketch geometry with constraints, then the solid features built on it; lengths are millimeters unless a unit is written):

FEATURE [PartDesign::SubShapeBinder] Binder
  BindCopyOnChange = 0
  BindMode = 0
  ClaimChildren = false
  Context = -> Body [Binder.]
  Fuse = false
  MakeFace = true
  OffsetFill = false
  OffsetIntersection = false
  OffsetJoinType = 0
  OffsetOpenResult = false
  PartialLoad = false
  Refine = true
  Relative = true
  Support = -> [Link]
  _Version = 2
FEATURE [Sketcher::SketchObject] Sketch
  ArcFitTolerance = 1e-06
  AttachmentSupport = -> [Origin]
  ExternalGeometry = -> [Binder]
  ExternalTypes = [0,0,0,0,0,0]
  FullyConstrained = true
  MakeInternals = false
  MapMode = 5
  sketch-geometry (13):
    g0: LineSegment [constr] StartX=20.0885 StartY=0 StartZ=0 EndX=24.4107 EndY=45.9046 EndZ=0
    g1: LineSegment [constr] StartX=20.0885 StartY=0 StartZ=0 EndX=24.4107 EndY=-45.9046 EndZ=0
    g2: LineSegment [constr] StartX=-15.4132 StartY=49.6542 StartZ=0 EndX=-20.0885 EndY=0 EndZ=0
    g3: LineSegment [constr] StartX=-20.0885 StartY=0 StartZ=0 EndX=-15.4132 EndY=-49.6542 EndZ=0
    g4: LineSegment [constr] StartX=-70.0371 StartY=51.7842 StartZ=0 EndX=268.466 EndY=19.9119 EndZ=0
    g5: LineSegment [constr] StartX=266.591 StartY=0 StartZ=0 EndX=268.466 EndY=19.9119 EndZ=0
    g6: LineSegment StartX=25.125 StartY=42.824 StartZ=0 EndX=21.0929 EndY=0 EndZ=0
    g7: LineSegment StartX=21.0929 StartY=0 StartZ=0 EndX=178.443 EndY=0 EndZ=0
    g8: LineSegment StartX=178.443 StartY=0 StartZ=0 EndX=181.093 EndY=28.1387 EndZ=0
    g9: LineSegment StartX=181.093 StartY=28.1387 StartZ=0 EndX=25.125 EndY=42.824 EndZ=0
    g10: Circle CenterX=34.1436 CenterY=31.9306 CenterZ=0 NormalX=0 NormalY=0 NormalZ=1 AngleXU=0 Radius=2.6
    g11: Circle CenterX=170.199 CenterY=19.1201 CenterZ=0 NormalX=0 NormalY=0 NormalZ=1 AngleXU=0 Radius=2.6
    g12: LineSegment [constr] StartX=34.1436 StartY=31.9306 StartZ=0 EndX=170.199 EndY=19.1201 EndZ=0
  constraints (38):
    c: PointOnObject(g0,g-1)
    c: PointOnObject(g0,g-3)
    c: Coincident(g1,g0)
    c: PointOnObject(g1,g-4)
    c: Perpendicular(g-4,g1)
    c: Perpendicular(g-3,g0)
    c: PointOnObject(g2,g-3)
    c: Coincident(g3,g2)
    c: PointOnObject(g3,g-4)
    c: Parallel(g2,g0)
    c: Parallel(g3,g1)
    c: Symmetric(g2,g0,g-1)
    c: Distance(g2,g0) = 40
    c: Coincident(g4,g-7)
    c: Coincident(g5,g-6)
    c: Coincident(g5,g4)
    c: Parallel(g4,g-3)
    c: PointOnObject(g4,g-8)
    c: PointOnObject(g6,g4)
    c: PointOnObject(g6,g-1)
    c: Coincident(g7,g6)
    c: PointOnObject(g7,g-1)
    c: Coincident(g8,g7)
    c: PointOnObject(g8,g4)
    c: Coincident(g9,g8)
    c: Coincident(g9,g6)
    c: Parallel(g6,g0)
    c: Parallel(g8,g6)
    c: Distance(g6,g0) = 1
    c: DistanceX(g6,g8) = 160
    c: Coincident(g12,g10)
    c: Coincident(g12,g11)
    c: Parallel(g12,g9)
    c: Equal(g11,g10)
    c: Diameter(g10) = 5.2
    c: Distance(g10,g6) = 10
    c: Distance(g11,g8) = 10
    c: Distance(g9,g12) = 10
FEATURE [PartDesign::Pad] Pad
  Direction = (0,0,1)
  Length = 8.2
  Length2 = 10
  Profile = -> Sketch
  ReferenceAxis = -> Sketch [N_Axis]
  Refine = true
  SideType = 0
  Suppressed = false
  Type = 0
  Type2 = 0
FEATURE [Sketcher::SketchObject] Sketch001
  ArcFitTolerance = 1e-06
  AttachmentSupport = -> [Pad]
  ExternalGeometry = -> [Pad,Binder]
  ExternalTypes = [0,0,0,0]
  FullyConstrained = true
  MakeInternals = false
  MapMode = 5
  Placement = pos=(0,0,0) rot=(1,0,0;3.14159rad)
  sketch-geometry (4):
    g0: LineSegment StartX=21.0929 StartY=0 StartZ=0 EndX=23.2502 EndY=-22.9121 EndZ=0
    g1: LineSegment StartX=23.2502 StartY=-22.9121 StartZ=0 EndX=179.218 EndY=-8.22672 EndZ=0
    g2: LineSegment StartX=179.218 StartY=-8.22672 StartZ=0 EndX=178.443 EndY=0 EndZ=0
    g3: LineSegment StartX=178.443 StartY=0 StartZ=0 EndX=21.0929 EndY=0 EndZ=0
  constraints (10):
    c: Coincident(g0,g-3)
    c: PointOnObject(g0,g-6)
    c: Coincident(g1,g0)
    c: PointOnObject(g1,g-6)
    c: Coincident(g2,g1)
    c: Coincident(g2,g-4)
    c: Coincident(g3,g2)
    c: Coincident(g3,g0)
    c: PointOnObject(g0,g-3)
    c: PointOnObject(g1,g-4)
FEATURE [PartDesign::Pad] Pad001
  BaseFeature = -> Pad
  Direction = (0,0,-1)
  Length = 2
  Length2 = 10
  Profile = -> Sketch001
  ReferenceAxis = -> Sketch001 [N_Axis]
  Refine = true
  SideType = 0
  Suppressed = false
  Type = 0
  Type2 = 0
FEATURE [Sketcher::SketchObject] Sketch002
  ArcFitTolerance = 1e-06
  AttachmentSupport = -> [Pad001]
  ExternalGeometry = -> [Pad001]
  ExternalTypes = [0,0]
  FullyConstrained = true
  MakeInternals = false
  MapMode = 5
  Placement = pos=(0,0,8.2) rot=(0,0,1;0rad)
  sketch-geometry (2):
    g0: Circle CenterX=34.1436 CenterY=31.9306 CenterZ=0 NormalX=0 NormalY=0 NormalZ=1 AngleXU=0 Radius=5
    g1: Circle CenterX=170.199 CenterY=19.1201 CenterZ=0 NormalX=0 NormalY=0 NormalZ=1 AngleXU=0 Radius=5
  constraints (4):
    c: Coincident(g0,g-3)
    c: Coincident(g1,g-4)
    c: Equal(g0,g1)
    c: Diameter(g1) = 10
FEATURE [PartDesign::Pocket] Pocket
  BaseFeature = -> Pad001
  Direction = (0,0,-1)
  Length = 1
  Length2 = 5
  Profile = -> Sketch002
  ReferenceAxis = -> Sketch002 [N_Axis]
  Refine = true
  SideType = 0
  Suppressed = false
  Type = 0
  Type2 = 0
FEATURE [PartDesign::Chamfer] Chamfer
  Angle = 45
  Base = -> Pocket [Edge1,Edge2]
  BaseFeature = -> Pocket
  ChamferType = 0
  FlipDirection = false
  Refine = true
  Size = 3
  Size2 = 1
  SupportTransform = false
  Suppressed = false
  UseAllEdges = false
FEATURE [PartDesign::Chamfer] Chamfer001
  Angle = 45
  Base = -> Chamfer [Edge21,Edge24]
  BaseFeature = -> Chamfer
  ChamferType = 0
  FlipDirection = false
  Refine = true
  Size = 2
  Size2 = 1
  SupportTransform = false
  Suppressed = false
  UseAllEdges = false
FEATURE [PartDesign::Mirrored] Mirrored
  BaseFeature = -> Chamfer001
  MirrorPlane = -> Chamfer001 [Face13]
  Refine = true
  Suppressed = false
  TransformMode = 1
FEATURE [PartDesign::Body] Body  label="lateral-carter-core"
  AllowCompound = true
  Group = -> [Binder,Sketch,Pad,Sketch001,Pad001,Sketch002,Pocket,Chamfer,Chamfer001,Mirrored]
  Origin = -> Origin
  Tip = -> Mirrored
FEATURE [PartDesign::SubShapeBinder] Binder001
  BindCopyOnChange = 0
  BindMode = 0
  ClaimChildren = false
  Context = -> Part [Body001.Binder001.]
  Fuse = false
  MakeFace = true
  OffsetFill = false
  OffsetIntersection = false
  OffsetJoinType = 0
  OffsetOpenResult = false
  PartialLoad = false
  Refine = true
  Relative = true
  Support = -> [Body[Mirrored.Face31]]
  _Version = 2
FEATURE [Sketcher::SketchObject] Sketch003
  ArcFitTolerance = 1e-06
  AttachmentSupport = -> [Binder001]
  ExternalGeometry = -> [Binder001]
  ExternalTypes = [0]
  FullyConstrained = false
  MakeInternals = false
  MapMode = 5
  Placement = pos=(0,0,-2) rot=(1,0,0;3.14159rad)
  sketch-geometry (20):
    g0: LineSegment StartX=24.1062 StartY=0 StartZ=0 EndX=25.933 EndY=-19.4025 EndZ=0
    g1: LineSegment StartX=25.933 StartY=-19.4025 StartZ=0 EndX=26.1973 EndY=-19.6213 EndZ=0
    g2: LineSegment StartX=26.1973 StartY=-19.6213 StartZ=0 EndX=175.708 EndY=-5.5439 EndZ=0
    g3: LineSegment StartX=175.927 StartY=-5.27958 StartZ=0 EndX=175.708 EndY=-5.5439 EndZ=0
    g4: LineSegment StartX=175.927 StartY=-5.27958 StartZ=0 EndX=175.457 EndY=-0.281226 EndZ=0
    g5: ArcOfCircle CenterX=178.443 CenterY=0 CenterZ=0 NormalX=0 NormalY=0 NormalZ=1 AngleXU=-1.47692 Radius=3 StartAngle=4.52463 EndAngle=4.71239
    g6: LineSegment StartX=175.927 StartY=5.27958 StartZ=0 EndX=175.457 EndY=0.281226 EndZ=0
    g7: LineSegment StartX=175.927 StartY=5.27958 StartZ=0 EndX=175.708 EndY=5.5439 EndZ=0
    g8: LineSegment StartX=26.1973 StartY=19.6213 StartZ=0 EndX=175.708 EndY=5.5439 EndZ=0
    g9: LineSegment StartX=25.933 StartY=19.4025 StartZ=0 EndX=26.1973 EndY=19.6213 EndZ=0
    g10: LineSegment StartX=24.1062 StartY=0 StartZ=0 EndX=25.933 EndY=19.4025 EndZ=0
    g11: LineSegment [constr] StartX=24.1062 StartY=0 StartZ=0 EndX=21.1194 EndY=-0.281226 EndZ=0
    g12: LineSegment [constr] StartX=25.933 StartY=-19.4025 StartZ=0 EndX=24.0199 EndY=-21.7133 EndZ=0
    g13: LineSegment [constr] StartX=26.1973 StartY=-19.6213 StartZ=0 EndX=26.4786 EndY=-22.6081 EndZ=0
    g14: LineSegment [constr] StartX=175.927 StartY=-5.27958 StartZ=0 EndX=178.238 EndY=-7.19271 EndZ=0
    g15: LineSegment [constr] StartX=175.927 StartY=-5.27958 StartZ=0 EndX=178.914 EndY=-4.99836 EndZ=0
    g16: LineSegment [constr] StartX=175.927 StartY=5.27958 StartZ=0 EndX=178.238 EndY=7.19271 EndZ=0
    g17: LineSegment [constr] StartX=26.1973 StartY=19.6213 StartZ=0 EndX=26.4786 EndY=22.6081 EndZ=0
    g18: LineSegment [constr] StartX=25.933 StartY=19.4025 StartZ=0 EndX=24.0199 EndY=21.7133 EndZ=0
    g19: LineSegment [constr] StartX=24.1062 StartY=0 StartZ=0 EndX=21.1194 EndY=0.281226 EndZ=0
  constraints (58):
    c: Coincident(g0,g1)
    c: Coincident(g0,g10)
    c: Coincident(g1,g2)
    c: Coincident(g2,g3)
    c: Coincident(g3,g4)
    c: Tangent(g4,g5) = 1.5708
    c: Tangent(g5,g6) = -1.5708
    c: Coincident(g6,g7)
    c: Coincident(g7,g8)
    c: Coincident(g8,g9)
    c: Coincident(g9,g10)
    c: Perpendicular(g11,g0)
    c: PointOnObject(g11,g0)
    c: PointOnObject(g11,g-3)
    c: Perpendicular(g12,g1)
    c: PointOnObject(g12,g1)
    c: PointOnObject(g12,g-4)
    c: Perpendicular(g13,g2)
    c: PointOnObject(g13,g2)
    c: PointOnObject(g13,g-5)
    c: Perpendicular(g14,g3)
    c: PointOnObject(g14,g3)
    c: PointOnObject(g14,g-6)
    c: Perpendicular(g15,g4)
    c: PointOnObject(g15,g4)
    c: PointOnObject(g15,g-7)
    c: Perpendicular(g16,g7)
    c: PointOnObject(g16,g7)
    c: PointOnObject(g16,g-9)
    c: Perpendicular(g17,g8)
    c: PointOnObject(g17,g8)
    c: PointOnObject(g17,g-10)
    c: Perpendicular(g18,g9)
    c: PointOnObject(g18,g9)
    c: PointOnObject(g18,g-11)
    c: Perpendicular(g19,g10)
    c: PointOnObject(g19,g10)
    c: PointOnObject(g19,g-12)
    c: Parallel(g10,g-12)
    c: Parallel(g0,g-3)
    c: Parallel(g1,g-4)
    c: Equal(g12,g11)
    c: Parallel(g2,g-5)
    c: Equal(g13,g11)
    c: Parallel(g3,g-6)
    c: Equal(g14,g11)
    c: Parallel(g4,g-7)
    c: Equal(g15,g11)
    c: Coincident(g5,g-8)
    c: Parallel(g6,g-8)
    c: Parallel(g7,g-9)
    c: Equal(g16,g11)
    c: Parallel(g8,g-10)
    c: Equal(g17,g11)
    c: Parallel(g9,g-11)
    c: Equal(g18,g11)
    c: Equal(g19,g11)
    c: Distance(g11) = 3
FEATURE [PartDesign::Pad] Pad002
  Direction = (0,0,-1)
  Length = 10
  Length2 = 10
  Profile = -> Sketch003
  ReferenceAxis = -> Sketch003 [N_Axis]
  Refine = true
  Reversed = true
  SideType = 0
  Suppressed = false
  Type = 0
  Type2 = 0
FEATURE [PartDesign::Body] Body001  label="lateral-carter-center"
  AllowCompound = true
  Group = -> [Binder001,Sketch003,Pad002]
  Origin = -> Origin002
  Tip = -> Pad002
COMPONENT P5 — recipe-attached ("lateral-rear-carter", modeled in this document).
Construction recipe (the document's own serialized feature program — sketch geometry with constraints, then the solid features built on it; lengths are millimeters unless a unit is written):

FEATURE [PartDesign::SubShapeBinder] Binder004
  BindCopyOnChange = 0
  BindMode = 0
  ClaimChildren = false
  Context = -> Part001 [Body003.Binder004.]
  Fuse = false
  MakeFace = true
  OffsetFill = false
  OffsetIntersection = false
  OffsetJoinType = 0
  OffsetOpenResult = false
  PartialLoad = false
  Refine = true
  Relative = true
  Support = -> [Link]
  _Version = 2
FEATURE [PartDesign::SubShapeBinder] Binder005
  BindCopyOnChange = 0
  BindMode = 0
  ClaimChildren = false
  Context = -> Part001 [Body003.Binder005.]
  Fuse = false
  MakeFace = true
  OffsetFill = false
  OffsetIntersection = false
  OffsetJoinType = 0
  OffsetOpenResult = false
  PartialLoad = false
  Refine = true
  Relative = true
  Support = -> [Part[Body.Mirrored.Face32]]
  _Version = 2
FEATURE [Sketcher::SketchObject] Sketch006
  ArcFitTolerance = 1e-06
  AttachmentSupport = -> [Origin008]
  ExternalGeometry = -> [Binder005,Binder004]
  ExternalTypes = [0,0,0,0,0,0,0]
  FullyConstrained = true
  MakeInternals = false
  MapMode = 5
  sketch-geometry (7):
    g0: LineSegment [constr] StartX=28.1118 StartY=42.5428 StartZ=0 EndX=-75 EndY=52.2515 EndZ=0
    g1: LineSegment [constr] StartX=-15.6944 StartY=46.6674 StartZ=0 EndX=-20.0885 EndY=0 EndZ=0
    g2: LineSegment StartX=-16.69 StartY=46.7612 StartZ=0 EndX=-21.0929 EndY=0 EndZ=0
    g3: LineSegment StartX=-71.9119 StartY=0 StartZ=0 EndX=-71.9119 EndY=31.8722 EndZ=0
    g4: LineSegment StartX=-71.9119 StartY=31.8722 StartZ=0 EndX=-70.0371 EndY=51.7842 EndZ=0
    g5: LineSegment StartX=-70.0371 StartY=51.7842 StartZ=0 EndX=-16.69 EndY=46.7612 EndZ=0
    g6: LineSegment StartX=-71.9119 StartY=0 StartZ=0 EndX=-21.0929 EndY=0 EndZ=0
  constraints (21):
    c: Coincident(g0,g-6)
    c: PointOnObject(g0,g-7)
    c: Parallel(g-6,g0)
    c: PointOnObject(g1,g0)
    c: PointOnObject(g1,g-1)
    c: Parallel(g1,g-3)
    c: Distance(g-3,g1) = 41
    c: PointOnObject(g2,g0)
    c: PointOnObject(g2,g-1)
    c: Coincident(g4,g3)
    c: PointOnObject(g4,g0)
    c: Coincident(g5,g4)
    c: Coincident(g5,g2)
    c: Parallel(g2,g1)
    c: Distance(g1,g2) = 1
    c: Perpendicular(g5,g4)
    c: Coincident(g3,g-9)
    c: PointOnObject(g3,g-1)
    c: Coincident(g6,g3)
    c: Coincident(g6,g2)
    c: Vertical(g3)
FEATURE [PartDesign::Pad] Pad004
  Direction = (0,0,1)
  Length = 8.2
  Length2 = 10
  Profile = -> Sketch006
  ReferenceAxis = -> Sketch006 [N_Axis]
  Refine = true
  SideType = 0
  Suppressed = false
  Type = 0
  Type2 = 0
FEATURE [PartDesign::Chamfer] Chamfer005
  Angle = 45
  Base = -> Pad004 [Edge5,Edge8]
  BaseFeature = -> Pad004
  ChamferType = 0
  FlipDirection = false
  Refine = true
  Size = 3
  Size2 = 1
  SupportTransform = false
  Suppressed = false
  UseAllEdges = false
FEATURE [PartDesign::Fillet] Fillet001
  Base = -> Chamfer005 [Edge14]
  BaseFeature = -> Chamfer005
  Radius = 7
  Refine = true
  SupportTransform = false
  Suppressed = false
  UseAllEdges = false
FEATURE [PartDesign::Mirrored] Mirrored002
  BaseFeature = -> Fillet001
  MirrorPlane = -> Fillet001 [Face9]
  Refine = true
  Suppressed = false
  TransformMode = 1
FEATURE [Sketcher::SketchObject] Sketch007
  ArcFitTolerance = 1e-06
  AttachmentSupport = -> [Mirrored002]
  ExternalGeometry = -> [Binder004]
  ExternalTypes = [0]
  FullyConstrained = true
  MakeInternals = false
  MapMode = 5
  Placement = pos=(0,0,8.2) rot=(0,0,1;0rad)
  sketch-geometry (1):
    g0: Circle CenterX=-62 CenterY=0 CenterZ=0 NormalX=0 NormalY=0 NormalZ=1 AngleXU=0 Radius=2.7
  constraints (3):
    c: PointOnObject(g0,g-1)
    c: Diameter(g0) = 5.4
    c: Distance(g0,g-3) = 10
FEATURE [PartDesign::Pocket] Pocket002
  BaseFeature = -> Mirrored002
  Direction = (0,0,-1)
  Length = 5
  Length2 = 5
  Profile = -> Sketch007
  ReferenceAxis = -> Sketch007 [N_Axis]
  Refine = true
  SideType = 0
  Suppressed = false
  Type = 1
  Type2 = 0
FEATURE [Sketcher::SketchObject] Sketch008
  ArcFitTolerance = 1e-06
  AttachmentSupport = -> [Pocket002]
  ExternalGeometry = -> [Pocket002]
  ExternalTypes = [0]
  FullyConstrained = true
  MakeInternals = false
  MapMode = 5
  Placement = pos=(0,0,8.2) rot=(0,0,1;0rad)
  sketch-geometry (1):
    g0: Circle CenterX=-62 CenterY=0 CenterZ=0 NormalX=0 NormalY=0 NormalZ=1 AngleXU=0 Radius=5
  constraints (2):
    c: Coincident(g0,g-3)
    c: Diameter(g0) = 10
FEATURE [PartDesign::Pocket] Pocket003
  BaseFeature = -> Pocket002
  Direction = (0,0,-1)
  Length = 1.5
  Length2 = 5
  Profile = -> Sketch008
  ReferenceAxis = -> Sketch008 [N_Axis]
  Refine = true
  SideType = 0
  Suppressed = false
  Type = 0
  Type2 = 0
FEATURE [Sketcher::SketchObject] Sketch009
  ArcFitTolerance = 1e-06
  AttachmentSupport = -> [Pocket003]
  ExternalGeometry = -> [Binder004,Pocket003]
  ExternalTypes = [0,0,0,0,0]
  FullyConstrained = true
  MakeInternals = false
  MapMode = 5
  Placement = pos=(0,0,0) rot=(1,0,0;3.14159rad)
  sketch-geometry (5):
    g0: LineSegment StartX=-18.5649 StartY=26.8493 StartZ=0 EndX=-52 EndY=29.9974 EndZ=0
    g1: LineSegment StartX=-52 StartY=29.9974 StartZ=0 EndX=-52 EndY=-29.9974 EndZ=0
    g2: LineSegment StartX=-52 StartY=-29.9974 StartZ=0 EndX=-18.5649 EndY=-26.8493 EndZ=0
    g3: LineSegment StartX=-18.5649 StartY=-26.8493 StartZ=0 EndX=-21.0929 EndY=0 EndZ=0
    g4: LineSegment StartX=-21.0929 StartY=0 StartZ=0 EndX=-18.5649 EndY=26.8493 EndZ=0
  constraints (14):
    c: PointOnObject(g0,g-6)
    c: PointOnObject(g0,g-3)
    c: Coincident(g1,g0)
    c: PointOnObject(g1,g-4)
    c: Vertical(g1)
    c: Coincident(g2,g1)
    c: PointOnObject(g2,g-5)
    c: Coincident(g3,g2)
    c: Coincident(g4,g3)
    c: Coincident(g4,g0)
    c: PointOnObject(g0,g-3)
    c: PointOnObject(g1,g-5)
    c: Coincident(g3,g-7)
    c: PointOnObject(g2,g-7)
FEATURE [PartDesign::Pad] Pad005
  BaseFeature = -> Pocket003
  Direction = (0,0,-1)
  Length = 2
  Length2 = 10
  Profile = -> Sketch009
  ReferenceAxis = -> Sketch009 [N_Axis]
  Refine = true
  SideType = 0
  Suppressed = false
  Type = 0
  Type2 = 0
FEATURE [PartDesign::ShapeBinder] CopyPad005
  Placement = pos=(0,0,-2) rot=(0,0,1;0rad)
  TraceSupport = false
FEATURE [Sketcher::SketchObject] Sketch010
  ArcFitTolerance = 1e-06
  AttachmentSupport = -> [CopyPad005]
  ExternalGeometry = -> [CopyPad005]
  ExternalTypes = [0]
  FullyConstrained = false
  MakeInternals = false
  MapMode = 5
  Placement = pos=(0,0,-2) rot=(1,0,0;3.14159rad)
  sketch-geometry (10):
    g0: LineSegment StartX=-21.8329 StartY=24.1437 StartZ=0 EndX=-49 EndY=26.7017 EndZ=0
    g1: LineSegment StartX=-49 StartY=26.7017 StartZ=0 EndX=-49 EndY=-26.7017 EndZ=0
    g2: LineSegment StartX=-49 StartY=-26.7017 StartZ=0 EndX=-21.8329 EndY=-24.1437 EndZ=0
    g3: LineSegment StartX=-21.8329 StartY=-24.1437 StartZ=0 EndX=-24.0797 EndY=-0.281226 EndZ=0
    g4: ArcOfCircle CenterX=-21.0929 CenterY=3.6e-15 CenterZ=0 NormalX=0 NormalY=0 NormalZ=1 AngleXU=-1.47692 Radius=3 StartAngle=4.52463 EndAngle=4.71239
    g5: LineSegment StartX=-24.0797 StartY=0.281226 StartZ=0 EndX=-21.8329 EndY=24.1437 EndZ=0
    g6: LineSegment [constr] StartX=-21.8329 StartY=24.1437 StartZ=0 EndX=-21.5516 EndY=27.1305 EndZ=0
    g7: LineSegment [constr] StartX=-49 StartY=26.7017 StartZ=0 EndX=-52 EndY=26.7017 EndZ=0
    g8: LineSegment [constr] StartX=-49 StartY=-26.7017 StartZ=0 EndX=-48.7188 EndY=-29.6884 EndZ=0
    g9: LineSegment [constr] StartX=-21.8329 StartY=-24.1437 StartZ=0 EndX=-18.8461 EndY=-23.8625 EndZ=0
  constraints (28):
    c: Coincident(g0,g1)
    c: Coincident(g0,g5)
    c: Coincident(g1,g2)
    c: Coincident(g2,g3)
    c: Tangent(g3,g4) = 1.5708
    c: Tangent(g4,g5) = 1.5708
    c: Perpendicular(g6,g0)
    c: PointOnObject(g6,g0)
    c: PointOnObject(g6,g-3)
    c: Perpendicular(g7,g1)
    c: PointOnObject(g7,g1)
    c: PointOnObject(g7,g-4)
    c: Perpendicular(g8,g2)
    c: PointOnObject(g8,g2)
    c: PointOnObject(g8,g-5)
    c: Perpendicular(g9,g3)
    c: PointOnObject(g9,g3)
    c: PointOnObject(g9,g-6)
    c: Parallel(g5,g-7)
    c: Parallel(g0,g-3)
    c: Parallel(g1,g-4)
    c: Equal(g7,g6)
    c: Parallel(g2,g-5)
    c: Equal(g8,g6)
    c: Parallel(g3,g-6)
    c: Equal(g9,g6)
    c: Coincident(g4,g-7)
    c: Distance(g6) = 3
FEATURE [PartDesign::Pad] Pad006
  Direction = (0,0,-1)
  Length = 12
  Length2 = 10
  Placement = pos=(0,0,-2) rot=(0,0,1;0rad)
  Profile = -> Sketch010
  ReferenceAxis = -> Sketch010 [N_Axis]
  Refine = true
  Reversed = true
  SideType = 0
  Suppressed = false
  Type = 0
  Type2 = 0
FEATURE [PartDesign::Body] Body004  label="lateral-rear-carter-center"
  AllowCompound = true
  Group = -> [CopyPad005,Sketch010,Pad006]
  Origin = -> Origin010
  Tip = -> Pad006
FEATURE [PartDesign::Pocket] Pocket005
  BaseFeature = -> Pad005
  Direction = (0,0,1)
  Length = 2
  Length2 = 5
  Profile = -> Pad005 [Face20]
  Refine = true
  SideType = 0
  Suppressed = false
  Type = 0
  Type2 = 0
FEATURE [PartDesign::Body] Body003  label="lateral-rear-carter-core"
  AllowCompound = true
  Group = -> [Binder004,Binder005,Sketch006,Pad004,Chamfer005,Fillet001,Mirrored002,Sketch007,Pocket002,Sketch008,Pocket003,Sketch009,Pad005,Pocket005]
  Origin = -> Origin008
  Tip = -> Pocket005
COMPONENT P6 — recipe-attached ("Part002", modeled in this document).
Construction recipe (the document's own serialized feature program — sketch geometry with constraints, then the solid features built on it; lengths are millimeters unless a unit is written):

FEATURE [Sketcher::SketchObject] Sketch011
  ArcFitTolerance = 1e-06
  AttachmentSupport = -> [Origin014]
  ExternalTypes = [0]
  FullyConstrained = true
  MakeInternals = false
  MapMode = 5
  Placement = pos=(0,0,0) rot=(1,0,0;1.5708rad)
  sketch-geometry (13):
    g0: LineSegment [constr] StartX=-78 StartY=-45 StartZ=0 EndX=78 EndY=-45 EndZ=0
    g1: LineSegment [constr] StartX=78 StartY=-45 StartZ=0 EndX=78 EndY=45 EndZ=0
    g2: LineSegment [constr] StartX=78 StartY=45 StartZ=0 EndX=-78 EndY=45 EndZ=0
    g3: LineSegment [constr] StartX=-78 StartY=45 StartZ=0 EndX=-78 EndY=-45 EndZ=0
    g4: GeomPoint [constr] X=0 Y=0 Z=0
    g5: LineSegment [constr] StartX=-78 StartY=-44.6 StartZ=0 EndX=78 EndY=-44.6 EndZ=0
    g6: LineSegment StartX=78 StartY=-44.6 StartZ=0 EndX=78 EndY=44.6 EndZ=0
    g7: LineSegment [constr] StartX=78 StartY=44.6 StartZ=0 EndX=-78 EndY=44.6 EndZ=0
    g8: LineSegment [constr] StartX=-78 StartY=44.6 StartZ=0 EndX=-78 EndY=-44.6 EndZ=0
    g9: GeomPoint [constr] X=0 Y=0 Z=0
    g10: LineSegment StartX=-6.1e-15 StartY=-44.6 StartZ=0 EndX=-6.1e-15 EndY=44.6 EndZ=0
    g11: LineSegment StartX=-6.1e-15 StartY=44.6 StartZ=0 EndX=78 EndY=44.6 EndZ=0
    g12: LineSegment StartX=-6.1e-15 StartY=-44.6 StartZ=0 EndX=78 EndY=-44.6 EndZ=0
  constraints (30):
    c: Coincident(g0,g1)
    c: Coincident(g1,g2)
    c: Coincident(g2,g3)
    c: Coincident(g3,g0)
    c: Horizontal(g0)
    c: Horizontal(g2)
    c: Vertical(g1)
    c: Vertical(g3)
    c: Symmetric(g2,g0,g4)
    c: Coincident(g4,g-1)
    c: DistanceX(g2,g2) = 156
    c: DistanceY(g1,g1) = 90
    c: Coincident(g5,g6)
    c: Coincident(g6,g7)
    c: Coincident(g7,g8)
    c: Coincident(g8,g5)
    c: Horizontal(g5)
    c: Horizontal(g7)
    c: Vertical(g6)
    c: Vertical(g8)
    c: Symmetric(g7,g5,g9)
    c: Coincident(g9,g4)
    c: PointOnObject(g6,g1)
    c: Distance(g6,g1) = 0.4
    c: Symmetric(g5,g5,g10)
    c: Symmetric(g7,g7,g10)
    c: Coincident(g11,g10)
    c: Coincident(g11,g6)
    c: Coincident(g12,g10)
    c: Coincident(g12,g5)
FEATURE [PartDesign::Pad] Pad007
  Direction = (0,-1,2e-16)
  Length = 3
  Length2 = 10
  Profile = -> Sketch011
  ReferenceAxis = -> Sketch011 [N_Axis]
  Refine = true
  SideType = 0
  Suppressed = false
  Type = 0
  Type2 = 0
FEATURE [Sketcher::SketchObject] Sketch012
  ArcFitTolerance = 1e-06
  AttachmentSupport = -> [Origin014]
  ExternalGeometry = -> [Pad007]
  ExternalTypes = [0,0]
  FullyConstrained = true
  MakeInternals = false
  MapMode = 5
  Placement = pos=(0,0,0) rot=(1,0,0;1.5708rad)
  sketch-geometry (4):
    g0: ArcOfCircle CenterX=74 CenterY=41.5 CenterZ=0 NormalX=0 NormalY=0 NormalZ=1 AngleXU=0 Radius=1.7 StartAngle=4.71239 EndAngle=7.85398
    g1: ArcOfCircle CenterX=70 CenterY=41.5 CenterZ=0 NormalX=0 NormalY=0 NormalZ=1 AngleXU=0 Radius=1.7 StartAngle=1.5708 EndAngle=4.71239
    g2: LineSegment StartX=74 StartY=39.8 StartZ=0 EndX=70 EndY=39.8 EndZ=0
    g3: LineSegment StartX=74 StartY=43.2 StartZ=0 EndX=70 EndY=43.2 EndZ=0
  constraints (10):
    c: Tangent(g0,g2) = 1.5708
    c: Tangent(g0,g3) = -1.5708
    c: Tangent(g1,g2) = 1.5708
    c: Tangent(g1,g3) = -1.5708
    c: Equal(g0,g1)
    c: Horizontal(g3)
    c: DistanceX(g1,g0) = 4
    c: Radius(g0) = 1.7
    c: Distance(g0,g-3) = 4
    c: DistanceY(g-1,g0) = 41.5
FEATURE [PartDesign::Pocket] Pocket004
  BaseFeature = -> Pad007
  Direction = (0,1,-2e-16)
  Length = 5
  Length2 = 5
  Profile = -> Sketch012
  ReferenceAxis = -> Sketch012 [N_Axis]
  Refine = true
  Reversed = true
  SideType = 0
  Suppressed = false
  Type = 0
  Type2 = 0
FEATURE [PartDesign::Mirrored] Mirrored004
  BaseFeature = -> Pocket004
  MirrorPlane = -> XY_Plane007
  Originals = -> [Pocket004]
  Refine = true
  Suppressed = false
  TransformMode = 0
FEATURE [PartDesign::Mirrored] Mirrored005
  BaseFeature = -> Mirrored004
  MirrorPlane = -> YZ_Plane007
  Refine = true
  Suppressed = false
  TransformMode = 1
FEATURE [PartDesign::Chamfer] Chamfer006
  Angle = 45
  Base = -> Mirrored005 [Edge1,Edge2,Edge6,Edge8]
  BaseFeature = -> Mirrored005
  ChamferType = 0
  FlipDirection = false
  Refine = true
  Size = 2
  Size2 = 1
  SupportTransform = false
  Suppressed = false
  UseAllEdges = false
FEATURE [Sketcher::SketchObject] Sketch013
  ArcFitTolerance = 1e-06
  AttachmentSupport = -> [Origin014]
  ExternalGeometry = -> [Chamfer006]
  ExternalTypes = [0]
  FullyConstrained = true
  MakeInternals = false
  MapMode = 5
  Placement = pos=(0,0,0) rot=(1,0,0;1.5708rad)
  sketch-geometry (5):
    g0: LineSegment StartX=93 StartY=-36.5 StartZ=0 EndX=93 EndY=36.5 EndZ=0
    g1: LineSegment StartX=93 StartY=36.5 StartZ=0 EndX=78 EndY=36.5 EndZ=0
    g2: LineSegment StartX=78 StartY=36.5 StartZ=0 EndX=78 EndY=-36.5 EndZ=0
    g3: LineSegment StartX=78 StartY=-36.5 StartZ=0 EndX=93 EndY=-36.5 EndZ=0
    g4: GeomPoint [constr] X=85.5 Y=0 Z=0
  constraints (13):
    c: Coincident(g0,g1)
    c: Coincident(g1,g2)
    c: Coincident(g2,g3)
    c: Coincident(g3,g0)
    c: Vertical(g0)
    c: Vertical(g2)
    c: Horizontal(g1)
    c: Horizontal(g3)
    c: Symmetric(g2,g0,g4)
    c: PointOnObject(g4,g-1)
    c: PointOnObject(g1,g-3)
    c: DistanceY(g0,g0) = 73
    c: DistanceX(g1,g1) = 15
FEATURE [PartDesign::Pad] Pad008
  BaseFeature = -> Chamfer006
  Direction = (0,-1,2e-16)
  Length = 3
  Length2 = 10
  Profile = -> Sketch013
  ReferenceAxis = -> Sketch013 [N_Axis]
  Refine = true
  SideType = 0
  Suppressed = false
  Type = 0
  Type2 = 0
FEATURE [PartDesign::Chamfer] Chamfer007
  Angle = 45
  Base = -> Pad008 [Edge15,Edge32]
  BaseFeature = -> Pad008
  ChamferType = 0
  FlipDirection = false
  Refine = true
  Size = 2
  Size2 = 1
  SupportTransform = false
  Suppressed = false
  UseAllEdges = false
FEATURE [Sketcher::SketchObject] Sketch014
  ArcFitTolerance = 1e-06
  AttachmentSupport = -> [Chamfer007]
  ExternalGeometry = -> [Chamfer007]
  ExternalTypes = [0,0]
  FullyConstrained = true
  MakeInternals = false
  MapMode = 5
  Placement = pos=(0,-3,0) rot=(1,0,0;1.5708rad)
  sketch-geometry (5):
    g0: LineSegment StartX=-75 StartY=-34.6 StartZ=0 EndX=75 EndY=-34.6 EndZ=0
    g1: LineSegment StartX=75 StartY=-34.6 StartZ=0 EndX=75 EndY=34.6 EndZ=0
    g2: LineSegment StartX=75 StartY=34.6 StartZ=0 EndX=-75 EndY=34.6 EndZ=0
    g3: LineSegment StartX=-75 StartY=34.6 StartZ=0 EndX=-75 EndY=-34.6 EndZ=0
    g4: GeomPoint [constr] X=0 Y=0 Z=0
  constraints (12):
    c: Coincident(g0,g1)
    c: Coincident(g1,g2)
    c: Coincident(g2,g3)
    c: Coincident(g3,g0)
    c: Horizontal(g0)
    c: Horizontal(g2)
    c: Vertical(g1)
    c: Vertical(g3)
    c: Symmetric(g2,g0,g4)
    c: Coincident(g4,g-1)
    c: Distance(g-3,g3) = 3
    c: Distance(g-4,g2) = 10
FEATURE [PartDesign::Pad] Pad009
  BaseFeature = -> Chamfer007
  Direction = (0,-1,2e-16)
  Length = 3
  Length2 = 10
  Profile = -> Sketch014
  ReferenceAxis = -> Sketch014 [N_Axis]
  Refine = true
  SideType = 0
  Suppressed = false
  Type = 0
  Type2 = 0
FEATURE [PartDesign::Fillet] Fillet002
  Base = -> Pad009 [Edge98,Edge96,Edge100,Edge95]
  BaseFeature = -> Pad009
  Radius = 5
  Refine = true
  SupportTransform = false
  Suppressed = false
  UseAllEdges = false
FEATURE [PartDesign::Body] Body005  label="top-carter-core"
  AllowCompound = true
  Group = -> [Sketch011,Pad007,Sketch012,Pocket004,Mirrored004,Mirrored005,Chamfer006,Sketch013,Pad008,Chamfer007,Sketch014,Pad009,Fillet002]
  Origin = -> Origin014
  Tip = -> Fillet002
FEATURE [PartDesign::SubShapeBinder] Binder006
  BindCopyOnChange = 0
  BindMode = 0
  ClaimChildren = false
  Context = -> Part002 [Body006.Binder006.]
  Fuse = false
  MakeFace = true
  OffsetFill = false
  OffsetIntersection = false
  OffsetJoinType = 0
  OffsetOpenResult = false
  PartialLoad = false
  Refine = true
  Relative = true
  Support = -> [Body005[Fillet002.Face40]]
  _Version = 2
FEATURE [Sketcher::SketchObject] Sketch015
  ArcFitTolerance = 1e-06
  AttachmentSupport = -> [Binder006]
  ExternalGeometry = -> [Binder006]
  ExternalTypes = [0]
  FullyConstrained = true
  MakeInternals = false
  MapMode = 5
  Placement = pos=(0,-6,0) rot=(1,0,0;1.5708rad)
  sketch-geometry (8):
    g0: LineSegment StartX=-70 StartY=-31.6 StartZ=0 EndX=70 EndY=-31.6 EndZ=0
    g1: ArcOfCircle CenterX=70 CenterY=-29.6 CenterZ=0 NormalX=0 NormalY=0 NormalZ=1 AngleXU=-1.5708 Radius=2 StartAngle=-1.901e-13 EndAngle=1.5708
    g2: LineSegment StartX=72 StartY=-29.6 StartZ=0 EndX=72 EndY=29.6 EndZ=0
    g3: ArcOfCircle CenterX=70 CenterY=29.6 CenterZ=0 NormalX=0 NormalY=0 NormalZ=1 AngleXU=-1.5708 Radius=2 StartAngle=1.5708 EndAngle=3.14159
    g4: LineSegment StartX=70 StartY=31.6 StartZ=0 EndX=-70 EndY=31.6 EndZ=0
    g5: ArcOfCircle CenterX=-70 CenterY=29.6 CenterZ=0 NormalX=0 NormalY=0 NormalZ=1 AngleXU=-1.5708 Radius=2 StartAngle=3.14159 EndAngle=4.71239
    g6: LineSegment StartX=-72 StartY=29.6 StartZ=0 EndX=-72 EndY=-29.6 EndZ=0
    g7: ArcOfCircle CenterX=-70 CenterY=-29.6 CenterZ=0 NormalX=0 NormalY=0 NormalZ=1 AngleXU=-1.5708 Radius=2 StartAngle=4.71239 EndAngle=6.28319
  constraints (16):
    c: Tangent(g0,g1) = -1.5708
    c: Tangent(g0,g7) = -1.5708
    c: Tangent(g1,g2) = -1.5708
    c: Tangent(g2,g3) = -1.5708
    c: Tangent(g3,g4) = -1.5708
    c: Tangent(g4,g5) = -1.5708
    c: Tangent(g5,g6) = -1.5708
    c: Tangent(g6,g7) = -1.5708
    c: Coincident(g7,g-4)
    c: Parallel(g0,g-3)
    c: Coincident(g1,g-5)
    c: Parallel(g2,g-7)
    c: Coincident(g3,g-9)
    c: Parallel(g4,g-10)
    c: Coincident(g5,g-8)
    c: Distance(g6,g-6) = 3
FEATURE [PartDesign::Pad] Pad010
  Direction = (0,-1,2e-16)
  Length = 6
  Length2 = 3
  Profile = -> Sketch015
  ReferenceAxis = -> Sketch015 [N_Axis]
  Refine = true
  Reversed = true
  SideType = 1
  Suppressed = false
  Type = 0
  Type2 = 0
FEATURE [PartDesign::Body] Body006  label="top-carter-center"
  AllowCompound = true
  Group = -> [Binder006,Sketch015,Pad010]
  Origin = -> Origin018
  Tip = -> Pad010
COMPONENT P7 — recipe-attached ("rear-carter", modeled in this document).
Construction recipe (the document's own serialized feature program — sketch geometry with constraints, then the solid features built on it; lengths are millimeters unless a unit is written):

FEATURE [PartDesign::SubShapeBinder] Binder007
  BindCopyOnChange = 0
  BindMode = 0
  ClaimChildren = false
  Context = -> Part003 [Body007.Binder007.]
  Fuse = false
  MakeFace = true
  OffsetFill = false
  OffsetIntersection = false
  OffsetJoinType = 0
  OffsetOpenResult = false
  PartialLoad = false
  Refine = true
  Relative = true
  Support = -> [Link]
  _Version = 2
FEATURE [Sketcher::SketchObject] Sketch016
  ArcFitTolerance = 1e-06
  AttachmentSupport = -> [Origin020]
  ExternalGeometry = -> [Binder007]
  ExternalTypes = [0,0,0,0]
  FullyConstrained = true
  MakeInternals = false
  MapMode = 5
  sketch-geometry (6):
    g0: LineSegment StartX=-70.0371 StartY=-51.7842 StartZ=0 EndX=-71.9119 EndY=-31.8722 EndZ=0
    g1: LineSegment StartX=-71.9119 StartY=-31.8722 StartZ=0 EndX=-71.9119 EndY=31.8722 EndZ=0
    g2: LineSegment StartX=-71.9119 StartY=31.8722 StartZ=0 EndX=-70.0371 EndY=51.7842 EndZ=0
    g3: LineSegment StartX=-70.0371 StartY=51.7842 StartZ=0 EndX=-79.9119 EndY=52.7139 EndZ=0
    g4: LineSegment StartX=-79.9119 StartY=52.7139 StartZ=0 EndX=-79.9119 EndY=-52.7139 EndZ=0
    g5: LineSegment StartX=-70.0371 StartY=-51.7842 StartZ=0 EndX=-79.9119 EndY=-52.7139 EndZ=0
  constraints (14):
    c: Coincident(g0,g-6)
    c: Coincident(g0,g-6)
    c: Coincident(g1,g0)
    c: Coincident(g1,g-3)
    c: Coincident(g2,g1)
    c: Coincident(g2,g-4)
    c: Coincident(g3,g2)
    c: Coincident(g4,g3)
    c: Vertical(g4)
    c: Coincident(g5,g0)
    c: Coincident(g5,g4)
    c: Tangent(g5,g-5)
    c: Tangent(g-4,g3)
    c: Distance(g1,g4) = 8
FEATURE [PartDesign::Pad] Pad011
  Direction = (0,0,1)
  Length = 140
  Length2 = 10
  Profile = -> Sketch016
  ReferenceAxis = -> Sketch016 [N_Axis]
  Refine = true
  SideType = 2
  Suppressed = false
  Type = 0
  Type2 = 0
FEATURE [Sketcher::SketchObject] Sketch017
  ArcFitTolerance = 1e-06
  AttachmentSupport = -> [Pad011]
  ExternalGeometry = -> [Pad011]
  ExternalTypes = [0,0]
  FullyConstrained = true
  MakeInternals = false
  MapMode = 5
  Placement = pos=(-74.2546,-6.99155,0) rot=(0.541233,0.594587,0.594587;2.14942rad)
  sketch-geometry (3):
    g0: Circle CenterX=-34.9907 CenterY=60 CenterZ=0 NormalX=0 NormalY=0 NormalZ=1 AngleXU=0 Radius=2.7
    g1: LineSegment [constr] StartX=-34.9907 StartY=70 StartZ=0 EndX=-34.9907 EndY=-70 EndZ=0
    g2: Circle CenterX=-34.9907 CenterY=-60 CenterZ=0 NormalX=0 NormalY=0 NormalZ=1 AngleXU=0 Radius=2.7
  constraints (7):
    c: Diameter(g0) = 5.4
    c: Symmetric(g-3,g-3,g1)
    c: Symmetric(g-4,g-4,g1)
    c: PointOnObject(g0,g1)
    c: Equal(g2,g0)
    c: Symmetric(g2,g0,g-1)
    c: Distance(g0,g-3) = 10
FEATURE [PartDesign::Pocket] Pocket006
  BaseFeature = -> Pad011
  Direction = (-0.995597,-0.0937419,0)
  Length = 12
  Length2 = 5
  Profile = -> Sketch017
  ReferenceAxis = -> Sketch017 [N_Axis]
  Refine = true
  SideType = 0
  Suppressed = false
  Type = 0
  Type2 = 0
FEATURE [Sketcher::SketchObject] Sketch018
  ArcFitTolerance = 1e-06
  AttachmentOffset = pos=(0,0,-6) rot=(0,0,1;0rad)
  AttachmentSupport = -> [Pocket006]
  ExternalGeometry = -> [Pocket006]
  ExternalTypes = [0,0]
  FullyConstrained = true
  MakeInternals = false
  MapMode = 5
  Placement = pos=(-80.2282,-7.554,0) rot=(0.541233,0.594587,0.594587;2.14942rad)
  sketch-geometry (2):
    g0: Circle CenterX=-34.9907 CenterY=60 CenterZ=0 NormalX=0 NormalY=0 NormalZ=1 AngleXU=0 Radius=5
    g1: Circle CenterX=-34.9907 CenterY=-60 CenterZ=0 NormalX=0 NormalY=0 NormalZ=1 AngleXU=0 Radius=5
  constraints (4):
    c: Coincident(g0,g-3)
    c: Coincident(g1,g-4)
    c: Equal(g1,g0)
    c: Diameter(g0) = 10
FEATURE [PartDesign::Pocket] Pocket007
  BaseFeature = -> Pocket006
  Direction = (-0.995597,-0.0937419,0)
  Length = 5
  Length2 = 5
  Profile = -> Sketch018
  ReferenceAxis = -> Sketch018 [N_Axis]
  Refine = true
  SideType = 0
  Suppressed = false
  Type = 0
  Type2 = 0
FEATURE [PartDesign::Mirrored] Mirrored006
  BaseFeature = -> Pocket007
  MirrorPlane = -> XZ_Plane010
  Originals = -> [Pocket006,Pocket007]
  Refine = true
  Suppressed = false
  TransformMode = 0
FEATURE [PartDesign::Chamfer] Chamfer008
  Angle = 45
  Base = -> Mirrored006 [Edge16,Edge12,Edge9,Edge8]
  BaseFeature = -> Mirrored006
  ChamferType = 0
  FlipDirection = false
  Refine = true
  Size = 3
  Size2 = 1
  SupportTransform = false
  Suppressed = false
  UseAllEdges = false
FEATURE [Sketcher::SketchObject] Sketch019
  ArcFitTolerance = 1e-06
  AttachmentSupport = -> [Chamfer008]
  ExternalGeometry = -> [Chamfer008]
  ExternalTypes = [0]
  FullyConstrained = true
  MakeInternals = false
  MapMode = 5
  Placement = pos=(-71.9119,0,0) rot=(0.57735,0.57735,0.57735;2.0944rad)
  sketch-geometry (13):
    g0: LineSegment StartX=-22.8722 StartY=-21.5 StartZ=0 EndX=-11.8722 EndY=-21.5 EndZ=0
    g1: LineSegment StartX=-11.8722 StartY=-21.5 StartZ=0 EndX=-11.8722 EndY=21.5 EndZ=0
    g2: LineSegment StartX=-11.8722 StartY=21.5 StartZ=0 EndX=-22.8722 EndY=21.5 EndZ=0
    g3: LineSegment StartX=-22.8722 StartY=21.5 StartZ=0 EndX=-22.8722 EndY=-21.5 EndZ=0
    g4: GeomPoint [constr] X=-17.3722 Y=0 Z=0
    g5: LineSegment [constr] StartX=-17.3722 StartY=21.5 StartZ=0 EndX=-17.3722 EndY=-21.5 EndZ=0
    g6: Circle CenterX=-17.3722 CenterY=26.5 CenterZ=0 NormalX=0 NormalY=0 NormalZ=1 AngleXU=0 Radius=1.55
    g7: Circle CenterX=-17.3722 CenterY=-26.5 CenterZ=0 NormalX=0 NormalY=0 NormalZ=1 AngleXU=0 Radius=1.55
    g8: LineSegment [constr] StartX=-29.8722 StartY=-32.5 StartZ=0 EndX=-4.87223 EndY=-32.5 EndZ=0
    g9: LineSegment [constr] StartX=-4.87223 StartY=-32.5 StartZ=0 EndX=-4.87223 EndY=32.5 EndZ=0
    g10: LineSegment [constr] StartX=-4.87223 StartY=32.5 StartZ=0 EndX=-29.8722 EndY=32.5 EndZ=0
    g11: LineSegment [constr] StartX=-29.8722 StartY=32.5 StartZ=0 EndX=-29.8722 EndY=-32.5 EndZ=0
    g12: GeomPoint [constr] X=-17.3722 Y=0 Z=0
  constraints (32):
    c: Coincident(g0,g1)
    c: Coincident(g1,g2)
    c: Coincident(g2,g3)
    c: Coincident(g3,g0)
    c: Horizontal(g0)
    c: Horizontal(g2)
    c: Vertical(g1)
    c: Vertical(g3)
    c: Symmetric(g2,g0,g4)
    c: PointOnObject(g4,g-1)
    c: DistanceY(g3,g3) = 43
    c: DistanceX(g2,g2) = 11
    c: Symmetric(g2,g2,g5)
    c: Symmetric(g0,g0,g5)
    c: Symmetric(g7,g6,g-1)
    c: Equal(g6,g7)
    c: Diameter(g7) = 3.1
    c: PointOnObject(g7,g5)
    c: Coincident(g8,g9)
    c: Coincident(g9,g10)
    c: Coincident(g10,g11)
    c: Coincident(g11,g8)
    c: Horizontal(g8)
    c: Horizontal(g10)
    c: Vertical(g9)
    c: Vertical(g11)
    c: Symmetric(g10,g8,g12)
    c: Coincident(g12,g4)
    c: DistanceX(g10,g10) = 25
    c: DistanceY(g11,g11) = 65
    c: Distance(g10,g-3) = 2
    c: DistanceY(g7,g6) = 53
FEATURE [PartDesign::Pocket] Pocket008
  BaseFeature = -> Chamfer008
  Direction = (-1,0,0)
  Length = 20
  Length2 = 5
  Profile = -> Sketch019
  ReferenceAxis = -> Sketch019 [N_Axis]
  Refine = true
  SideType = 0
  Suppressed = false
  Type = 0
  Type2 = 0
FEATURE [PartDesign::Chamfer] Chamfer009
  Angle = 45
  Base = -> Pocket008 [Edge43,Edge45]
  BaseFeature = -> Pocket008
  ChamferType = 0
  FlipDirection = false
  Refine = true
  Size = 5
  Size2 = 1
  SupportTransform = false
  Suppressed = false
  UseAllEdges = false
FEATURE [PartDesign::Chamfer] Chamfer010
  Angle = 45
  Base = -> Chamfer009 [Edge7,Edge2]
  BaseFeature = -> Chamfer009
  ChamferType = 0
  FlipDirection = false
  Refine = true
  Size = 2
  Size2 = 1
  SupportTransform = false
  Suppressed = false
  UseAllEdges = false
FEATURE [PartDesign::SubShapeBinder] Binder008
  BindCopyOnChange = 0
  BindMode = 0
  ClaimChildren = false
  Context = -> Part003 [Body007.Binder008.]
  Fuse = false
  MakeFace = true
  OffsetFill = false
  OffsetIntersection = false
  OffsetJoinType = 0
  OffsetOpenResult = false
  PartialLoad = false
  Refine = true
  Relative = true
  Support = -> [Link001[Fillet001.Face2]]
  _Version = 2
FEATURE [Sketcher::SketchObject] Sketch020
  ArcFitTolerance = 1e-06
  AttachmentSupport = -> [Chamfer010]
  ExternalGeometry = -> [Binder008]
  ExternalTypes = [0,0,0]
  FullyConstrained = true
  MakeInternals = false
  MapMode = 5
  Placement = pos=(-71.9119,0,0) rot=(0.57735,0.57735,0.57735;2.0944rad)
  sketch-geometry (5):
    g0: Circle CenterX=16.8 CenterY=24 CenterZ=0 NormalX=0 NormalY=0 NormalZ=1 AngleXU=0 Radius=1.6
    g1: Circle CenterX=16.8 CenterY=-24 CenterZ=0 NormalX=0 NormalY=0 NormalZ=1 AngleXU=0 Radius=1.6
    g2: Circle CenterX=20.8 CenterY=10 CenterZ=0 NormalX=0 NormalY=0 NormalZ=1 AngleXU=0 Radius=6
    g3: Circle CenterX=20.8 CenterY=-10 CenterZ=0 NormalX=0 NormalY=0 NormalZ=1 AngleXU=0 Radius=6
    g4: LineSegment [constr] StartX=26.8 StartY=10 StartZ=0 EndX=20.8 EndY=10 EndZ=0
  constraints (11):
    c: Coincident(g0,g-3)
    c: Coincident(g1,g-4)
    c: Equal(g1,g0)
    c: Diameter(g0) = 3.2
    c: Equal(g3,g2)
    c: Symmetric(g2,g3,g-1)
    c: Diameter(g2) = 12
    c: Symmetric(g-5,g-5,g4)
    c: Coincident(g4,g2)
    c: Horizontal(g4)
    c: Distance(g4,g4) = 6
FEATURE [PartDesign::Pocket] Pocket009
  BaseFeature = -> Chamfer010
  Direction = (-1,0,0)
  Length = 14
  Length2 = 5
  Profile = -> Sketch020
  ReferenceAxis = -> Sketch020 [N_Axis]
  Refine = true
  SideType = 0
  Suppressed = false
  Type = 0
  Type2 = 0
FEATURE [PartDesign::Chamfer] Chamfer011
  Angle = 45
  Base = -> Pocket009 [Edge11,Edge14]
  BaseFeature = -> Pocket009
  ChamferType = 1
  FlipDirection = false
  Refine = true
  Size = 3
  Size2 = 6
  SupportTransform = false
  Suppressed = false
  UseAllEdges = false
FEATURE [PartDesign::Chamfer] Chamfer012
  Angle = 45
  Base = -> Chamfer011 [Edge14,Edge11,Edge13,Edge20]
  BaseFeature = -> Chamfer011
  ChamferType = 0
  FlipDirection = false
  Refine = true
  Size = 0.4
  Size2 = 1
  SupportTransform = false
  Suppressed = false
  UseAllEdges = false
FEATURE [PartDesign::Body] Body007  label="rear-carter-core"
  AllowCompound = true
  Group = -> [Binder007,Sketch016,Pad011,Sketch017,Pocket006,Sketch018,Pocket007,Mirrored006,Chamfer008,Sketch019,Pocket008,Chamfer009,Chamfer010,Binder008,Sketch020,Pocket009,Chamfer011,Chamfer012]
  Origin = -> Origin020
  Tip = -> Chamfer012
FEATURE [PartDesign::ShapeBinder] CopyChamfer012
  TraceSupport = false
FEATURE [Sketcher::SketchObject] Sketch021
  ArcFitTolerance = 1e-06
  AttachmentSupport = -> [CopyChamfer012]
  ExternalGeometry = -> [CopyChamfer012]
  ExternalTypes = [0,0]
  FullyConstrained = true
  MakeInternals = false
  MapMode = 5
  Placement = pos=(-79.9119,0,0) rot=(0.57735,-0.57735,-0.57735;2.0944rad)
  sketch-geometry (5):
    g0: LineSegment StartX=-29.7139 StartY=67 StartZ=0 EndX=-29.7139 EndY=37 EndZ=0
    g1: LineSegment StartX=-29.7139 StartY=37 StartZ=0 EndX=29.7139 EndY=37 EndZ=0
    g2: LineSegment StartX=29.7139 StartY=37 StartZ=0 EndX=29.7139 EndY=67 EndZ=0
    g3: LineSegment StartX=29.7139 StartY=67 StartZ=0 EndX=-29.7139 EndY=67 EndZ=0
    g4: GeomPoint [constr] X=0 Y=52 Z=0
  constraints (13):
    c: Coincident(g0,g1)
    c: Coincident(g1,g2)
    c: Coincident(g2,g3)
    c: Coincident(g3,g0)
    c: Vertical(g0)
    c: Vertical(g2)
    c: Horizontal(g1)
    c: Horizontal(g3)
    c: Symmetric(g2,g0,g4)
    c: PointOnObject(g4,g-2)
    c: Distance(g2,g-3) = 3
    c: Distance(g0,g0) = 30
    c: Distance(g-4,g0) = 23
FEATURE [PartDesign::Pad] Pad012
  Direction = (-1,0,0)
  Length = 5
  Length2 = 5
  Profile = -> Sketch021
  ReferenceAxis = -> Sketch021 [N_Axis]
  Refine = true
  Reversed = true
  SideType = 0
  Suppressed = false
  Type = 0
  Type2 = 0
FEATURE [PartDesign::Mirrored] Mirrored007
  BaseFeature = -> Pad012
  MirrorPlane = -> XY_Plane012
  Originals = -> [Pad012]
  Refine = true
  Suppressed = false
  TransformMode = 1
FEATURE [PartDesign::Fillet] Fillet003
  Base = -> Mirrored007 [Edge8,Edge5,Edge1,Edge14,Edge17,Edge2,Edge13,Edge20]
  BaseFeature = -> Mirrored007
  Radius = 3
  Refine = true
  SupportTransform = false
  Suppressed = false
  UseAllEdges = false
FEATURE [PartDesign::Body] Body008  label="rear-carter-center"
  AllowCompound = true
  Group = -> [CopyChamfer012,Sketch021,Pad012,Mirrored007,Fillet003]
  Origin = -> Origin024
  Tip = -> Fillet003
PROVENANCE & LICENSES
A FreeCAD (.FCStd) document from a public repository crawl; recipes are the document's own serialized feature recipes (and, for linked parts, companion documents' recipes).
License: as declared in the source repository (recorded in the dataset sidecar).
